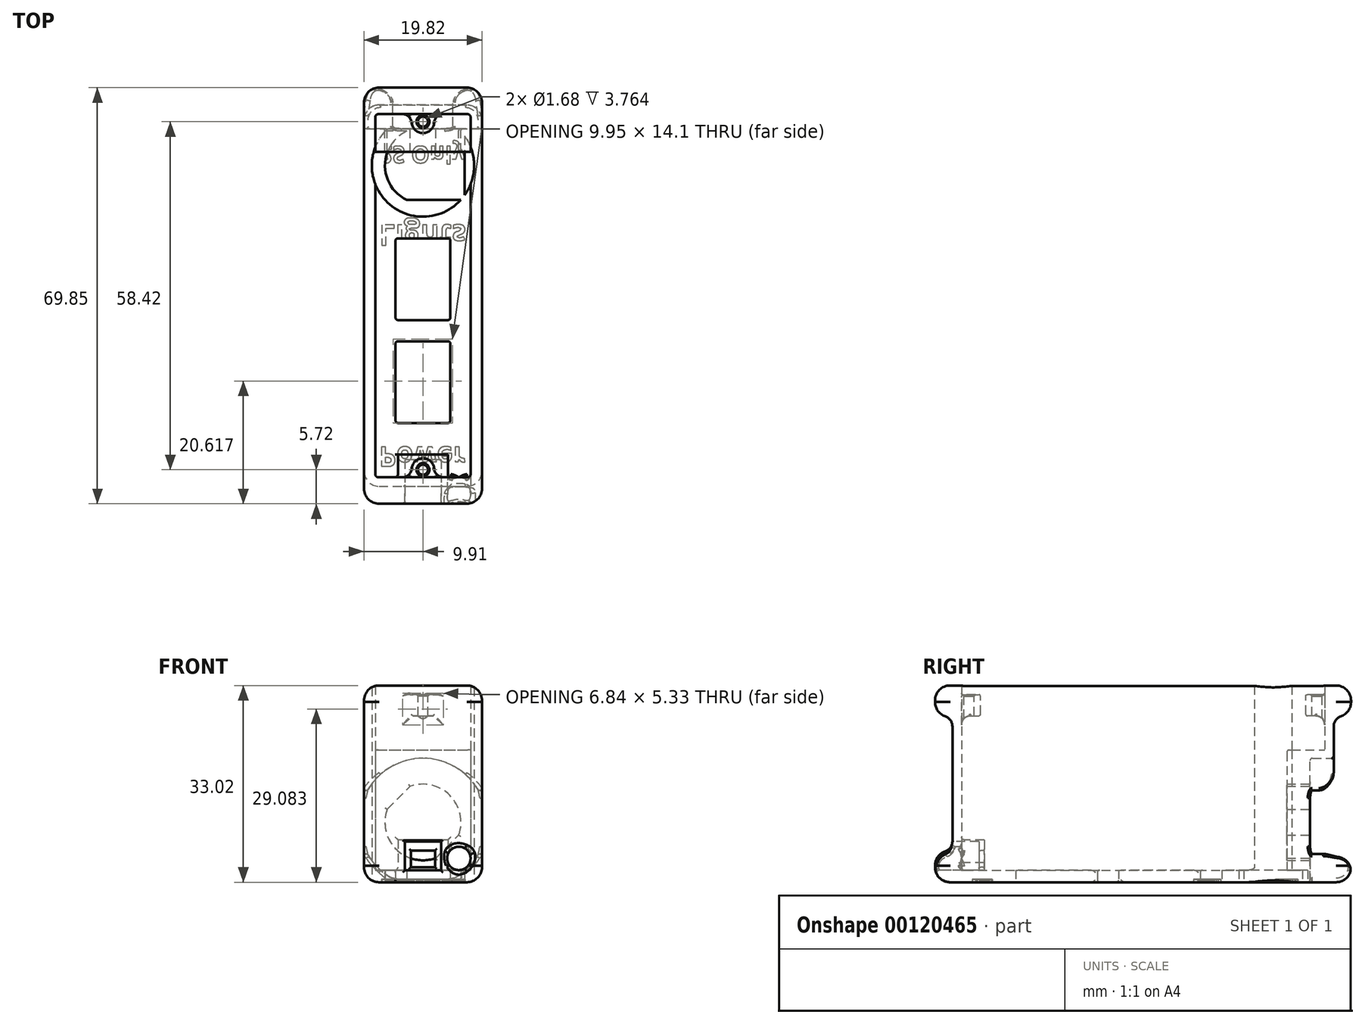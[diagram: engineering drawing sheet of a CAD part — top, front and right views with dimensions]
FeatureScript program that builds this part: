
annotation { "Feature Type Name" : "Feature", "Feature Type Description" : "" }
export const myFeature = defineFeature(function(context is Context, id is Id, definition is map)
    precondition{}
    {
        {
            var Q0;
            Q0=qCreatedBy(makeId("Top.planeOp"),FACE);
            var sketch = newSketch(context, id + "F0", { "sketchPlane" : qUnion([Q0])});
            skLineSegment(sketch, "E0.bottom", {"start": v(8, 30.48) * mm, "end": v(-8, 30.48) * mm});
            skLineSegment(sketch, "E0.top", {"start": v(8, -30.48) * mm, "end": v(-8, -30.48) * mm});
            skLineSegment(sketch, "E0.left", {"start": v(8, 30.48) * mm, "end": v(8, -30.48) * mm});
            skLineSegment(sketch, "E0.right", {"start": v(-8, 30.48) * mm, "end": v(-8, -30.48) * mm});
            skPoint(sketch, "E0.middle", {"position": v(0, 0) * mm});
            skLineSegment(sketch, "E1.bottom", {"start": v(9.9, 32.38) * mm, "end": v(-9.9, 32.38) * mm});
            skLineSegment(sketch, "E1.top", {"start": v(9.9, -32.38) * mm, "end": v(-9.9, -32.38) * mm});
            skLineSegment(sketch, "E1.left", {"start": v(9.9, 32.38) * mm, "end": v(9.9, -32.38) * mm});
            skLineSegment(sketch, "E1.right", {"start": v(-9.9, 32.38) * mm, "end": v(-9.9, -32.38) * mm});
            skCircle(sketch, "E2", {"center": v(0, 21.84) * mm, "radius": 6.38 * mm});
            skLineSegment(sketch, "E3.bottom", {"start": v(7.02, 27.62) * mm, "end": v(-7.02, 27.62) * mm});
            skLineSegment(sketch, "E3.top", {"start": v(7.02, 16.07) * mm, "end": v(-7.02, 16.07) * mm});
            skLineSegment(sketch, "E3.left", {"start": v(7.02, 27.62) * mm, "end": v(7.02, 16.07) * mm});
            skLineSegment(sketch, "E3.right", {"start": v(-7.02, 27.62) * mm, "end": v(-7.02, 16.07) * mm});
            skLineSegment(sketch, "E4.bottom", {"start": v(4.6, 9.63) * mm, "end": v(-4.6, 9.63) * mm});
            skLineSegment(sketch, "E4.top", {"start": v(4.6, -4.09) * mm, "end": v(-4.6, -4.09) * mm});
            skLineSegment(sketch, "E4.left", {"start": v(4.6, 9.63) * mm, "end": v(4.6, -4.09) * mm});
            skLineSegment(sketch, "E4.right", {"start": v(-4.6, 9.63) * mm, "end": v(-4.6, -4.09) * mm});
            skPoint(sketch, "E4.middle", {"position": v(0, 2.77) * mm});
            skCircle(sketch, "E5", {"center": v(0, 21.84) * mm, "radius": 8.59 * mm});
            skLineSegment(sketch, "E6.bottom", {"start": v(4.6, -7.65) * mm, "end": v(-4.6, -7.65) * mm});
            skLineSegment(sketch, "E6.top", {"start": v(4.6, -21.36) * mm, "end": v(-4.6, -21.36) * mm});
            skLineSegment(sketch, "E6.left", {"start": v(4.6, -7.65) * mm, "end": v(4.6, -21.36) * mm});
            skLineSegment(sketch, "E6.right", {"start": v(-4.6, -7.65) * mm, "end": v(-4.6, -21.36) * mm});
            skPoint(sketch, "E6.middle", {"position": v(0, -14.5) * mm});
            skSolve(sketch);
        }
        {
            var Q0;
            Q0 = qSketchRegion(id + "F0", true);
            var Q1;
            {var subQ0=sQuery(id+"F0.wireOp",EDGE,"E5");var subQ1=sQuery(id+"F0.wireOp",EDGE,"E0.right");var subQ2=makeQuery(id+"F0.imprint","INTERSECT",VERTEX,{"disambiguationData":[OD(0.0)],"derivedFrom":[subQ1,subQ0]});Q1=makeQuery(id+"F0.imprint","IMPRINT",FACE,{"disambiguationData":[TD([[makeQuery(id+"F0.imprint","IMPRINT",EDGE,{"disambiguationData":[TD([[subQ2,-1.0]])],"derivedFrom":subQ1}),-1.0]])]});}
            var Q2;
            {var subQ0=sQuery(id+"F0.wireOp",EDGE,"E5");var subQ1=sQuery(id+"F0.wireOp",EDGE,"E0.left");var subQ2=makeQuery(id+"F0.imprint","INTERSECT",VERTEX,{"disambiguationData":[OD(0.0)],"derivedFrom":[subQ1,subQ0]});Q2=makeQuery(id+"F0.imprint","IMPRINT",FACE,{"disambiguationData":[TD([[makeQuery(id+"F0.imprint","IMPRINT",EDGE,{"disambiguationData":[TD([[subQ2,-1.0]])],"derivedFrom":subQ1}),1.0]])]});}
            var Q3;
            {var subQ1=sQuery(id+"F0.wireOp",EDGE,"E0.bottom");Q3=makeQuery(id+"F0.imprint","IMPRINT",FACE,{"disambiguationData":[TD([[makeQuery(id+"F0.imprint","IMPRINT",EDGE,{"derivedFrom":subQ1}),1.0]])]});}
            var Q4;
            {var subQ0=sQuery(id+"F0.wireOp",EDGE,"E3.bottom");var subQ1=sQuery(id+"F0.wireOp",EDGE,"E2");var subQ2=makeQuery(id+"F0.imprint","INTERSECT",VERTEX,{"disambiguationData":[OD(0.0)],"derivedFrom":[subQ1,subQ0]});Q4=makeQuery(id+"F0.imprint","IMPRINT",FACE,{"disambiguationData":[TD([[makeQuery(id+"F0.imprint","IMPRINT",EDGE,{"disambiguationData":[TD([[subQ2,1.0]])],"derivedFrom":subQ1}),-1.0]])]});}
            var Q5;
            {var subQ0=sQuery(id+"F0.wireOp",EDGE,"E3.bottom");var subQ1=sQuery(id+"F0.wireOp",EDGE,"E2");var subQ2=makeQuery(id+"F0.imprint","INTERSECT",VERTEX,{"disambiguationData":[OD(0.0)],"derivedFrom":[subQ1,subQ0]});Q5=makeQuery(id+"F0.imprint","IMPRINT",FACE,{"disambiguationData":[TD([[makeQuery(id+"F0.imprint","IMPRINT",EDGE,{"disambiguationData":[TD([[subQ2,1.0]])],"derivedFrom":subQ1}),1.0]])]});}
            var Q6;
            {var subQ1=sQuery(id+"F0.wireOp",EDGE,"E2");var subQ5=sQuery(id+"F0.wireOp",EDGE,"E3.bottom");var subQ6=makeQuery(id+"F0.imprint","INTERSECT",VERTEX,{"disambiguationData":[OD(0.0)],"derivedFrom":[subQ1,subQ5]});Q6=makeQuery(id+"F0.imprint","IMPRINT",FACE,{"disambiguationData":[TD([[makeQuery(id+"F0.imprint","IMPRINT",EDGE,{"disambiguationData":[TD([[subQ6,-1.0]])],"derivedFrom":subQ1}),-1.0]])]});}
            var Q7;
            {var subQ0=sQuery(id+"F0.wireOp",EDGE,"E5");var subQ1=sQuery(id+"F0.wireOp",EDGE,"E0.right");var subQ2=makeQuery(id+"F0.imprint","INTERSECT",VERTEX,{"disambiguationData":[OD(0.0)],"derivedFrom":[subQ1,subQ0]});Q7=makeQuery(id+"F0.imprint","IMPRINT",FACE,{"disambiguationData":[TD([[makeQuery(id+"F0.imprint","IMPRINT",EDGE,{"disambiguationData":[TD([[subQ2,-1.0]])],"derivedFrom":subQ1}),1.0]])]});}
            var Q8;
            {var subQ0=sQuery(id+"F0.wireOp",EDGE,"E3.top");var subQ1=sQuery(id+"F0.wireOp",EDGE,"E2");var subQ2=makeQuery(id+"F0.imprint","INTERSECT",VERTEX,{"disambiguationData":[OD(0.0)],"derivedFrom":[subQ1,subQ0]});Q8=makeQuery(id+"F0.imprint","IMPRINT",FACE,{"disambiguationData":[TD([[makeQuery(id+"F0.imprint","IMPRINT",EDGE,{"disambiguationData":[TD([[subQ2,-1.0]])],"derivedFrom":subQ1}),-1.0]])]});}
            var Q9;
            {var subQ0=sQuery(id+"F0.wireOp",EDGE,"E3.right");var subQ1=sQuery(id+"F0.wireOp",EDGE,"E3.top");var subQ2=makeQuery(id+"F0.imprint","INTERSECT",VERTEX,{"derivedFrom":[subQ1,subQ0]});Q9=makeQuery(id+"F0.imprint","IMPRINT",FACE,{"disambiguationData":[TD([[makeQuery(id+"F0.imprint","IMPRINT",EDGE,{"disambiguationData":[TD([[subQ2,1.0]])],"derivedFrom":subQ1}),-1.0]])]});}
            var Q10;
            {var subQ0=sQuery(id+"F0.wireOp",EDGE,"E3.right");var subQ1=sQuery(id+"F0.wireOp",EDGE,"E3.bottom");var subQ2=makeQuery(id+"F0.imprint","INTERSECT",VERTEX,{"derivedFrom":[subQ1,subQ0]});Q10=makeQuery(id+"F0.imprint","IMPRINT",FACE,{"disambiguationData":[TD([[makeQuery(id+"F0.imprint","IMPRINT",EDGE,{"disambiguationData":[TD([[subQ2,1.0]])],"derivedFrom":subQ1}),1.0]])]});}
            var Q11;
            {var subQ0=sQuery(id+"F0.wireOp",EDGE,"E3.left");var subQ1=sQuery(id+"F0.wireOp",EDGE,"E3.bottom");var subQ2=makeQuery(id+"F0.imprint","INTERSECT",VERTEX,{"derivedFrom":[subQ1,subQ0]});Q11=makeQuery(id+"F0.imprint","IMPRINT",FACE,{"disambiguationData":[TD([[makeQuery(id+"F0.imprint","IMPRINT",EDGE,{"disambiguationData":[TD([[subQ2,-1.0]])],"derivedFrom":subQ1}),1.0]])]});}
            var Q12;
            {var subQ0=sQuery(id+"F0.wireOp",EDGE,"E5");var subQ1=sQuery(id+"F0.wireOp",EDGE,"E0.left");var subQ2=makeQuery(id+"F0.imprint","INTERSECT",VERTEX,{"disambiguationData":[OD(0.0)],"derivedFrom":[subQ1,subQ0]});Q12=makeQuery(id+"F0.imprint","IMPRINT",FACE,{"disambiguationData":[TD([[makeQuery(id+"F0.imprint","IMPRINT",EDGE,{"disambiguationData":[TD([[subQ2,-1.0]])],"derivedFrom":subQ1}),-1.0]])]});}
            var Q13;
            {var subQ1=sQuery(id+"F0.wireOp",EDGE,"E2");var subQ5=sQuery(id+"F0.wireOp",EDGE,"E3.bottom");var subQ6=makeQuery(id+"F0.imprint","INTERSECT",VERTEX,{"disambiguationData":[OD(1.0)],"derivedFrom":[subQ1,subQ5]});Q13=makeQuery(id+"F0.imprint","IMPRINT",FACE,{"disambiguationData":[TD([[makeQuery(id+"F0.imprint","IMPRINT",EDGE,{"disambiguationData":[TD([[subQ6,1.0]])],"derivedFrom":subQ1}),-1.0]])]});}
            var Q14;
            {var subQ0=sQuery(id+"F0.wireOp",EDGE,"E3.top");var subQ1=sQuery(id+"F0.wireOp",EDGE,"E2");var subQ2=makeQuery(id+"F0.imprint","INTERSECT",VERTEX,{"disambiguationData":[OD(0.0)],"derivedFrom":[subQ1,subQ0]});Q14=makeQuery(id+"F0.imprint","IMPRINT",FACE,{"disambiguationData":[TD([[makeQuery(id+"F0.imprint","IMPRINT",EDGE,{"disambiguationData":[TD([[subQ2,-1.0]])],"derivedFrom":subQ1}),1.0]])]});}
            var Q15;
            {var subQ0=sQuery(id+"F0.wireOp",EDGE,"E3.left");var subQ1=sQuery(id+"F0.wireOp",EDGE,"E3.top");var subQ2=makeQuery(id+"F0.imprint","INTERSECT",VERTEX,{"derivedFrom":[subQ1,subQ0]});Q15=makeQuery(id+"F0.imprint","IMPRINT",FACE,{"disambiguationData":[TD([[makeQuery(id+"F0.imprint","IMPRINT",EDGE,{"disambiguationData":[TD([[subQ2,-1.0]])],"derivedFrom":subQ1}),-1.0]])]});}
            var Q16;
            {var subQ8=sQuery(id+"F0.wireOp",EDGE,"E0.top");Q16=makeQuery(id+"F0.imprint","IMPRINT",FACE,{"disambiguationData":[TD([[makeQuery(id+"F0.imprint","IMPRINT",EDGE,{"derivedFrom":subQ8}),-1.0]])]});}
            var Q17;
            {var subQ0=sQuery(id+"F0.wireOp",EDGE,"E3.bottom");var subQ1=sQuery(id+"F0.wireOp",EDGE,"E2");var subQ2=makeQuery(id+"F0.imprint","INTERSECT",VERTEX,{"disambiguationData":[OD(0.0)],"derivedFrom":[subQ1,subQ0]});Q17=makeQuery(id+"F0.imprint","IMPRINT",FACE,{"disambiguationData":[TD([[makeQuery(id+"F0.imprint","IMPRINT",EDGE,{"disambiguationData":[TD([[subQ2,-1.0]])],"derivedFrom":subQ1}),1.0]])]});}
            extrude(context, id + "F1", {"entities" : qUnion([Q0, Q1, Q2, Q3, Q4, Q5, Q6, Q7, Q8, Q9, Q10, Q11, Q12, Q13, Q14, Q15, Q16, Q17]), "depth" : 2.03 * mm});
        }
        {
            var Q0;
            {var subQ4=sQuery(id+"F0.wireOp",EDGE,"E0.bottom");Q0=makeQuery(id+"F0.imprint","IMPRINT",FACE,{"disambiguationData":[TD([[makeQuery(id+"F0.imprint","IMPRINT",EDGE,{"derivedFrom":subQ4}),-1.0]])]});}
            var Q1;
            {var subQ0=sQuery(id+"F0.wireOp",EDGE,"E5");var subQ1=sQuery(id+"F0.wireOp",EDGE,"E0.left");var subQ2=makeQuery(id+"F0.imprint","INTERSECT",VERTEX,{"disambiguationData":[OD(0.0)],"derivedFrom":[subQ1,subQ0]});Q1=makeQuery(id+"F0.imprint","IMPRINT",FACE,{"disambiguationData":[TD([[makeQuery(id+"F0.imprint","IMPRINT",EDGE,{"disambiguationData":[TD([[subQ2,-1.0]])],"derivedFrom":subQ1}),1.0]])]});}
            var Q2;
            {var subQ0=sQuery(id+"F0.wireOp",EDGE,"E5");var subQ1=sQuery(id+"F0.wireOp",EDGE,"E0.right");var subQ2=makeQuery(id+"F0.imprint","INTERSECT",VERTEX,{"disambiguationData":[OD(0.0)],"derivedFrom":[subQ1,subQ0]});Q2=makeQuery(id+"F0.imprint","IMPRINT",FACE,{"disambiguationData":[TD([[makeQuery(id+"F0.imprint","IMPRINT",EDGE,{"disambiguationData":[TD([[subQ2,-1.0]])],"derivedFrom":subQ1}),-1.0]])]});}
            extrude(context, id + "F2", {"entities" : qUnion([Q0, Q1, Q2]), "operationType" : NewBodyOperationType.ADD, "depth" : 33.02 * mm});
        }
        {
            var Q0;
            Q0=makeQuery(id+"F2.opExtrude","CAP_FACE",FACE,{"disambiguationData":[OSD([sQuery(id+"F0.wireOp",EDGE,"E0.bottom"),sQuery(id+"F0.wireOp",EDGE,"E0.top"),sQuery(id+"F0.wireOp",EDGE,"E0.left"),sQuery(id+"F0.wireOp",EDGE,"E0.right"),sQuery(id+"F0.wireOp",EDGE,"E1.bottom"),sQuery(id+"F0.wireOp",EDGE,"E1.top"),sQuery(id+"F0.wireOp",EDGE,"E1.left"),sQuery(id+"F0.wireOp",EDGE,"E1.right")])],"isStart":false});
            var sketch = newSketch(context, id + "F3", { "sketchPlane" : qUnion([Q0])});
            skCircle(sketch, "E7", {"center": v(0, 29.21) * mm, "radius": 1.9 * mm});
            skCircle(sketch, "E8", {"center": v(0, -29.21) * mm, "radius": 1.9 * mm});
            skCircle(sketch, "E9", {"center": v(0, -29.21) * mm, "radius": 0.84 * mm});
            skCircle(sketch, "E10", {"center": v(0, 29.21) * mm, "radius": 0.84 * mm});
            skSolve(sketch);
        }
        {
            var Q0;
            Q0 = qSketchRegion(id + "F3", true);
            extrude(context, id + "F4", {"entities" : qUnion([Q0]), "operationType" : NewBodyOperationType.ADD, "oppositeDirection" : true, "depth" : 5.08 * mm});
        }
        {
            var Q0;
            {var subQ0=sQuery(id+"F0.wireOp",EDGE,"E1.bottom");Q0=makeQuery(id+"F2.boolean.opBoolean","MERGE",FACE,{"derivedFrom":[makeQuery(id+"F1.opExtrude","SWEPT_FACE",FACE,{"disambiguationData":[OSD([subQ0])]}),makeQuery(id+"F2.opExtrude","SWEPT_FACE",FACE,{"disambiguationData":[OSD([subQ0])]})]});}
            extrude(context, id + "F5", {"entities" : qUnion([Q0]), "operationType" : NewBodyOperationType.ADD, "depth" : 2.54 * mm});
        }
        {
            var Q0;
            {var subQ0=sQuery(id+"F0.wireOp",EDGE,"E1.top");Q0=makeQuery(id+"F2.boolean.opBoolean","MERGE",FACE,{"derivedFrom":[makeQuery(id+"F1.opExtrude","SWEPT_FACE",FACE,{"disambiguationData":[OSD([subQ0])]}),makeQuery(id+"F2.opExtrude","SWEPT_FACE",FACE,{"disambiguationData":[OSD([subQ0])]})]});}
            extrude(context, id + "F6", {"entities" : qUnion([Q0]), "operationType" : NewBodyOperationType.ADD, "depth" : 2.54 * mm});
        }
        {
            var Q0;
            Q0=qCreatedBy(makeId("Right.planeOp"),FACE);
            var sketch = newSketch(context, id + "F7", { "sketchPlane" : qUnion([Q0])});
            skLineSegment(sketch, "E11.bottom", {"start": v(38.48, 27.94) * mm, "end": v(33.78, 27.94) * mm});
            skLineSegment(sketch, "E11.top", {"start": v(38.48, 5.08) * mm, "end": v(33.78, 5.08) * mm});
            skLineSegment(sketch, "E11.left", {"start": v(38.48, 27.94) * mm, "end": v(38.48, 5.08) * mm});
            skLineSegment(sketch, "E11.right", {"start": v(32, 26.16) * mm, "end": v(32, 6.86) * mm});
            skLineSegment(sketch, "E12.bottom", {"start": v(-39.14, 27.94) * mm, "end": v(-33.78, 27.94) * mm});
            skLineSegment(sketch, "E12.top", {"start": v(-39.14, 5.08) * mm, "end": v(-33.78, 5.08) * mm});
            skLineSegment(sketch, "E12.left", {"start": v(-39.14, 27.94) * mm, "end": v(-39.14, 5.08) * mm});
            skLineSegment(sketch, "E12.right", {"start": v(-32, 26.16) * mm, "end": v(-32, 6.86) * mm});
            skPoint(sketch, "E13.visualSharp", {"position": v(32, 27.94) * mm});
            skArc(sketch, "E13.filletArc", {"start": v(33.78, 27.94) * mm, "mid": v(32.52, 27.42) * mm, "end": v(32, 26.16) * mm});
            skPoint(sketch, "E14.visualSharp", {"position": v(32, 5.08) * mm});
            skArc(sketch, "E14.filletArc", {"start": v(32, 6.86) * mm, "mid": v(32.52, 5.6) * mm, "end": v(33.78, 5.08) * mm});
            skPoint(sketch, "E15.visualSharp", {"position": v(-32, 5.08) * mm});
            skArc(sketch, "E15.filletArc", {"start": v(-33.78, 5.08) * mm, "mid": v(-32.52, 5.6) * mm, "end": v(-32, 6.86) * mm});
            skPoint(sketch, "E16.visualSharp", {"position": v(-32, 27.94) * mm});
            skArc(sketch, "E16.filletArc", {"start": v(-32, 26.16) * mm, "mid": v(-32.52, 27.42) * mm, "end": v(-33.78, 27.94) * mm});
            skSolve(sketch);
        }
        {
            var Q0;
            Q0 = qSketchRegion(id + "F7", true);
            extrude(context, id + "F8", {"entities" : qUnion([Q0]), "operationType" : NewBodyOperationType.REMOVE, "endBound" : BoundingType.SYMMETRIC, "oppositeDirection" : true, "depth" : 25.4 * mm});
        }
        {
            var Q0;
            Q0=makeQuery(id+"F2.opExtrude","SWEPT_FACE",FACE,{"disambiguationData":[OSD([sQuery(id+"F0.wireOp",EDGE,"E0.bottom")])]});
            var sketch = newSketch(context, id + "F9", { "sketchPlane" : qUnion([Q0])});
            skCircle(sketch, "E17", {"center": v(0, 10.07) * mm, "radius": 6.39 * mm});
            skLineSegment(sketch, "E18.bottom", {"start": v(-8, 2.03) * mm, "end": v(8, 2.03) * mm});
            skLineSegment(sketch, "E18.top", {"start": v(-8, 22.17) * mm, "end": v(8, 22.17) * mm});
            skLineSegment(sketch, "E18.left", {"start": v(-8, 2.03) * mm, "end": v(-8, 22.17) * mm});
            skLineSegment(sketch, "E18.right", {"start": v(8, 2.03) * mm, "end": v(8, 22.17) * mm});
            skSolve(sketch);
        }
        {
            var Q0;
            Q0=qCreatedBy(makeId("Front.planeOp"),FACE);
            cPlane(context, id + "F10", {"entities" : qUnion([Q0]), "cplaneType" : CPlaneType.OFFSET, "offset" : 38.1 * mm, "oppositeDirection" : true, "width" : 152.4 * mm, "height" : 152.4 * mm});
        }
        {
            var Q0;
            Q0=qCreatedBy(id+"F10.planeOp",FACE);
            var sketch = newSketch(context, id + "F11", { "sketchPlane" : qUnion([Q0])});
            skCircle(sketch, "E19", {"center": v(0, 10.07) * mm, "radius": 6.39 * mm});
            skCircle(sketch, "E20", {"center": v(0, 10.07) * mm, "radius": 10.73 * mm});
            skLineSegment(sketch, "E21", {"start": v(-1.17, 0.73) * mm, "end": v(9.04, 10.94) * mm});
            skLineSegment(sketch, "E22", {"start": v(-1.17, 0.73) * mm, "end": v(-9.34, 8.9) * mm});
            skLineSegment(sketch, "E23", {"start": v(-9.34, 8.9) * mm, "end": v(0.87, 19.11) * mm});
            skLineSegment(sketch, "E24", {"start": v(0.87, 19.11) * mm, "end": v(9.04, 10.94) * mm});
            skSolve(sketch);
        }
        {
            var Q0;
            {var subQ1=sQuery(id+"F0.wireOp",EDGE,"E1.left");var subQ2=sQuery(id+"F0.wireOp",EDGE,"E1.top");Q0=makeQuery(id+"F8.boolean.opBoolean","SPLIT",EDGE,{"disambiguationData":[TD([makeQuery(id+"F8.opExtrude","SWEPT_FACE",FACE,{"disambiguationData":[OSD([sQuery(id+"F7.wireOp",EDGE,"E12.top")])]})])],"derivedFrom":makeQuery(id+"F6.opExtrude","CAP_EDGE",EDGE,{"disambiguationData":[OSD([subQ2,subQ1])],"isStart":false})});}
            var Q1;
            {var subQ0=sQuery(id+"F0.wireOp",EDGE,"E1.left");var subQ1=sQuery(id+"F0.wireOp",EDGE,"E1.top");Q1=makeQuery(id+"F8.boolean.opBoolean","SPLIT",EDGE,{"disambiguationData":[TD([makeQuery(id+"F8.opExtrude","SWEPT_FACE",FACE,{"disambiguationData":[OSD([sQuery(id+"F7.wireOp",EDGE,"E12.bottom")])]})])],"derivedFrom":makeQuery(id+"F6.opExtrude","CAP_EDGE",EDGE,{"disambiguationData":[OSD([subQ1,subQ0])],"isStart":false})});}
            var Q2;
            {var subQ0=sQuery(id+"F0.wireOp",EDGE,"E1.top");var subQ1=sQuery(id+"F0.wireOp",EDGE,"E1.right");Q2=makeQuery(id+"F8.boolean.opBoolean","SPLIT",EDGE,{"disambiguationData":[TD([makeQuery(id+"F8.opExtrude","SWEPT_FACE",FACE,{"disambiguationData":[OSD([sQuery(id+"F7.wireOp",EDGE,"E12.bottom")])]})])],"derivedFrom":makeQuery(id+"F6.opExtrude","CAP_EDGE",EDGE,{"disambiguationData":[OSD([subQ0,subQ1])],"isStart":false})});}
            var Q3;
            {var subQ1=sQuery(id+"F0.wireOp",EDGE,"E1.right");var subQ2=sQuery(id+"F0.wireOp",EDGE,"E1.top");Q3=makeQuery(id+"F8.boolean.opBoolean","SPLIT",EDGE,{"disambiguationData":[TD([makeQuery(id+"F8.opExtrude","SWEPT_FACE",FACE,{"disambiguationData":[OSD([sQuery(id+"F7.wireOp",EDGE,"E12.top")])]})])],"derivedFrom":makeQuery(id+"F6.opExtrude","CAP_EDGE",EDGE,{"disambiguationData":[OSD([subQ2,subQ1])],"isStart":false})});}
            var Q4;
            {var subQ0=sQuery(id+"F0.wireOp",EDGE,"E1.bottom");var subQ1=sQuery(id+"F0.wireOp",EDGE,"E1.right");Q4=makeQuery(id+"F8.boolean.opBoolean","SPLIT",EDGE,{"disambiguationData":[TD([makeQuery(id+"F8.opExtrude","SWEPT_FACE",FACE,{"disambiguationData":[OSD([sQuery(id+"F7.wireOp",EDGE,"E11.top")])]})])],"derivedFrom":makeQuery(id+"F5.opExtrude","CAP_EDGE",EDGE,{"disambiguationData":[OSD([subQ0,subQ1])],"isStart":false})});}
            var Q5;
            {var subQ0=sQuery(id+"F0.wireOp",EDGE,"E1.bottom");var subQ1=sQuery(id+"F0.wireOp",EDGE,"E1.left");Q5=makeQuery(id+"F8.boolean.opBoolean","SPLIT",EDGE,{"disambiguationData":[TD([makeQuery(id+"F8.opExtrude","SWEPT_FACE",FACE,{"disambiguationData":[OSD([sQuery(id+"F7.wireOp",EDGE,"E11.top")])]})])],"derivedFrom":makeQuery(id+"F5.opExtrude","CAP_EDGE",EDGE,{"disambiguationData":[OSD([subQ0,subQ1])],"isStart":false})});}
            var Q6;
            {var subQ0=sQuery(id+"F0.wireOp",EDGE,"E1.right");var subQ2=sQuery(id+"F0.wireOp",EDGE,"E1.bottom");Q6=makeQuery(id+"F8.boolean.opBoolean","SPLIT",EDGE,{"disambiguationData":[TD([makeQuery(id+"F8.opExtrude","SWEPT_FACE",FACE,{"disambiguationData":[OSD([sQuery(id+"F7.wireOp",EDGE,"E11.bottom")])]})])],"derivedFrom":makeQuery(id+"F5.opExtrude","CAP_EDGE",EDGE,{"disambiguationData":[OSD([subQ2,subQ0])],"isStart":false})});}
            var Q7;
            {var subQ0=sQuery(id+"F0.wireOp",EDGE,"E1.left");var subQ2=sQuery(id+"F0.wireOp",EDGE,"E1.bottom");Q7=makeQuery(id+"F8.boolean.opBoolean","SPLIT",EDGE,{"disambiguationData":[TD([makeQuery(id+"F8.opExtrude","SWEPT_FACE",FACE,{"disambiguationData":[OSD([sQuery(id+"F7.wireOp",EDGE,"E11.bottom")])]})])],"derivedFrom":makeQuery(id+"F5.opExtrude","CAP_EDGE",EDGE,{"disambiguationData":[OSD([subQ2,subQ0])],"isStart":false})});}
            fillet(context, id + "F12", {"entities" : qUnion([Q0, Q1, Q2, Q3, Q4, Q5, Q6, Q7]), "radius" : 2.54 * mm, "tangentPropagation" : true, "allowEdgeOverflow" : false});
        }
        {
            var Q0;
            Q0 = qSketchRegion(id + "F9", true);
            var Q1;
            Q1=makeQuery(id+"F9.imprint","IMPRINT",FACE,{"disambiguationData":[TD([[makeQuery(id+"F9.imprint","IMPRINT",EDGE,{"derivedFrom":sQuery(id+"F9.wireOp",EDGE,"E17")}),1.0]])]});
            extrude(context, id + "F13", {"entities" : qUnion([Q0, Q1]), "operationType" : NewBodyOperationType.ADD, "depth" : 6.35 * mm});
        }
        {
            var Q0;
            Q0=makeQuery(id+"F11.imprint","IMPRINT",FACE,{"disambiguationData":[TD([[makeQuery(id+"F11.imprint","IMPRINT",EDGE,{"derivedFrom":sQuery(id+"F11.wireOp",EDGE,"E19")}),1.0]])]});
            var Q1;
            Q1=makeQuery(id+"F13.opExtrude","CAP_FACE",FACE,{"disambiguationData":[OSD([sQuery(id+"F9.wireOp",EDGE,"E18.bottom"),sQuery(id+"F9.wireOp",EDGE,"E18.top"),sQuery(id+"F9.wireOp",EDGE,"E18.left"),sQuery(id+"F9.wireOp",EDGE,"E18.right")])],"isStart":false});
            extrude(context, id + "F14", {"entities" : qUnion([Q0]), "operationType" : NewBodyOperationType.REMOVE, "endBound" : BoundingType.UP_TO_SURFACE, "endBoundEntityFace" : qUnion([Q1]), "depth" : 25.4 * mm});
        }
        {
            var Q0;
            {var subQ0=sQuery(id+"F0.wireOp",EDGE,"E1.right");Q0=makeQuery(id+"F8.boolean.opBoolean","INTERSECT",EDGE,{"derivedFrom":[makeQuery(id+"F6.boolean.opBoolean","MERGE",FACE,{"derivedFrom":[makeQuery(id+"F5.boolean.opBoolean","MERGE",FACE,{"derivedFrom":[makeQuery(id+"F2.boolean.opBoolean","MERGE",FACE,{"derivedFrom":[makeQuery(id+"F1.opExtrude","SWEPT_FACE",FACE,{"disambiguationData":[OSD([subQ0])]}),makeQuery(id+"F2.opExtrude","SWEPT_FACE",FACE,{"disambiguationData":[OSD([subQ0])]})]}),makeQuery(id+"F5.opExtrude","SWEPT_FACE",FACE,{"disambiguationData":[OSD([sQuery(id+"F0.wireOp",EDGE,"E1.bottom"),subQ0])]})]}),makeQuery(id+"F6.opExtrude","SWEPT_FACE",FACE,{"disambiguationData":[OSD([sQuery(id+"F0.wireOp",EDGE,"E1.top"),subQ0])]})]}),makeQuery(id+"F8.opExtrude","SWEPT_FACE",FACE,{"disambiguationData":[OSD([sQuery(id+"F7.wireOp",EDGE,"E11.right")])]})]});}
            var Q1;
            {var subQ0=sQuery(id+"F0.wireOp",EDGE,"E1.right");Q1=makeQuery(id+"F8.boolean.opBoolean","INTERSECT",EDGE,{"derivedFrom":[makeQuery(id+"F6.boolean.opBoolean","MERGE",FACE,{"derivedFrom":[makeQuery(id+"F5.boolean.opBoolean","MERGE",FACE,{"derivedFrom":[makeQuery(id+"F2.boolean.opBoolean","MERGE",FACE,{"derivedFrom":[makeQuery(id+"F1.opExtrude","SWEPT_FACE",FACE,{"disambiguationData":[OSD([subQ0])]}),makeQuery(id+"F2.opExtrude","SWEPT_FACE",FACE,{"disambiguationData":[OSD([subQ0])]})]}),makeQuery(id+"F5.opExtrude","SWEPT_FACE",FACE,{"disambiguationData":[OSD([sQuery(id+"F0.wireOp",EDGE,"E1.bottom"),subQ0])]})]}),makeQuery(id+"F6.opExtrude","SWEPT_FACE",FACE,{"disambiguationData":[OSD([sQuery(id+"F0.wireOp",EDGE,"E1.top"),subQ0])]})]}),makeQuery(id+"F8.opExtrude","SWEPT_FACE",FACE,{"disambiguationData":[OSD([sQuery(id+"F7.wireOp",EDGE,"E12.right")])]})]});}
            fillet(context, id + "F15", {"entities" : qUnion([Q0, Q1]), "radius" : 2.54 * mm, "tangentPropagation" : true, "allowEdgeOverflow" : false});
        }
        {
            var Q0;
            {var subQ0=sQuery(id+"F0.wireOp",EDGE,"E1.left");var subQ1=sQuery(id+"F0.wireOp",EDGE,"E1.top");var subQ2=sQuery(id+"F0.wireOp",EDGE,"E1.bottom");Q0=makeQuery(id+"F6.boolean.opBoolean","MERGE",EDGE,{"derivedFrom":[makeQuery(id+"F5.boolean.opBoolean","MERGE",EDGE,{"derivedFrom":[makeQuery(id+"F2.opExtrude","CAP_EDGE",EDGE,{"disambiguationData":[OSD([subQ0])],"isStart":false}),makeQuery(id+"F5.opExtrude","SWEPT_EDGE",EDGE,{"disambiguationData":[OSD([subQ2,subQ0]),TDD([makeQuery(id+"F2.opExtrude","CAP_VERTEX",VERTEX,{"disambiguationData":[OSD([subQ2,subQ0])],"isStart":false})])]})]}),makeQuery(id+"F6.opExtrude","SWEPT_EDGE",EDGE,{"disambiguationData":[OSD([subQ1,subQ0]),TDD([makeQuery(id+"F2.opExtrude","CAP_VERTEX",VERTEX,{"disambiguationData":[OSD([subQ1,subQ0])],"isStart":false})])]})]});}
            var Q1;
            {var subQ0=sQuery(id+"F0.wireOp",EDGE,"E1.right");var subQ1=sQuery(id+"F0.wireOp",EDGE,"E1.top");var subQ2=sQuery(id+"F0.wireOp",EDGE,"E1.bottom");Q1=makeQuery(id+"F6.boolean.opBoolean","MERGE",EDGE,{"derivedFrom":[makeQuery(id+"F5.boolean.opBoolean","MERGE",EDGE,{"derivedFrom":[makeQuery(id+"F1.opExtrude","CAP_EDGE",EDGE,{"disambiguationData":[OSD([subQ0])],"isStart":true}),makeQuery(id+"F5.opExtrude","SWEPT_EDGE",EDGE,{"disambiguationData":[OSD([subQ2,subQ0]),TDD([makeQuery(id+"F1.opExtrude","CAP_VERTEX",VERTEX,{"disambiguationData":[OSD([subQ2,subQ0])],"isStart":true})])]})]}),makeQuery(id+"F6.opExtrude","SWEPT_EDGE",EDGE,{"disambiguationData":[OSD([subQ1,subQ0]),TDD([makeQuery(id+"F1.opExtrude","CAP_VERTEX",VERTEX,{"disambiguationData":[OSD([subQ1,subQ0])],"isStart":true})])]})]});}
            fillet(context, id + "F16", {"entities" : qUnion([Q0, Q1]), "radius" : 2.54 * mm, "tangentPropagation" : true, "allowEdgeOverflow" : false});
        }
        {
            var Q0;
            Q0 = qSketchRegion(id + "F11", true);
            var Q1;
            {var subQ5=sQuery(id+"F11.wireOp",EDGE,"E22");Q1=makeQuery(id+"F11.imprint","IMPRINT",FACE,{"disambiguationData":[TD([[makeQuery(id+"F11.imprint","IMPRINT",EDGE,{"derivedFrom":subQ5}),-1.0]])]});}
            var Q2;
            {var subQ5=sQuery(id+"F11.wireOp",EDGE,"E24");Q2=makeQuery(id+"F11.imprint","IMPRINT",FACE,{"disambiguationData":[TD([[makeQuery(id+"F11.imprint","IMPRINT",EDGE,{"derivedFrom":subQ5}),-1.0]])]});}
            var Q3;
            {var subQ0=sQuery(id+"F11.wireOp",EDGE,"E21");var subQ1=sQuery(id+"F11.wireOp",EDGE,"E19");var subQ2=makeQuery(id+"F11.imprint","INTERSECT",VERTEX,{"disambiguationData":[OD(0.0)],"derivedFrom":[subQ1,subQ0]});Q3=makeQuery(id+"F11.imprint","IMPRINT",FACE,{"disambiguationData":[TD([[makeQuery(id+"F11.imprint","IMPRINT",EDGE,{"disambiguationData":[TD([[subQ2,-1.0]])],"derivedFrom":subQ1}),1.0]])]});}
            var Q4;
            {var subQ0=sQuery(id+"F11.wireOp",EDGE,"E23");var subQ1=sQuery(id+"F11.wireOp",EDGE,"E19");var subQ2=makeQuery(id+"F11.imprint","INTERSECT",VERTEX,{"disambiguationData":[OD(0.0)],"derivedFrom":[subQ1,subQ0]});Q4=makeQuery(id+"F11.imprint","IMPRINT",FACE,{"disambiguationData":[TD([[makeQuery(id+"F11.imprint","IMPRINT",EDGE,{"disambiguationData":[TD([[subQ2,1.0]])],"derivedFrom":subQ1}),1.0]])]});}
            var Q5;
            {var subQ0=sQuery(id+"F11.wireOp",EDGE,"E23");var subQ1=sQuery(id+"F11.wireOp",EDGE,"E19");var subQ2=makeQuery(id+"F11.imprint","INTERSECT",VERTEX,{"disambiguationData":[OD(0.0)],"derivedFrom":[subQ1,subQ0]});Q5=makeQuery(id+"F11.imprint","IMPRINT",FACE,{"disambiguationData":[TD([[makeQuery(id+"F11.imprint","IMPRINT",EDGE,{"disambiguationData":[TD([[subQ2,-1.0]])],"derivedFrom":subQ1}),1.0]])]});}
            extrude(context, id + "F17", {"entities" : qUnion([Q0, Q1, Q2, Q3, Q4, Q5]), "operationType" : NewBodyOperationType.REMOVE, "depth" : 10.06 * mm});
        }
        {
            var Q0;
            Q0=makeQuery(id+"F4.boolean.opBoolean","INTERSECT",EDGE,{"disambiguationData":[OD(0.0)],"derivedFrom":[makeQuery(id+"F2.opExtrude","SWEPT_FACE",FACE,{"disambiguationData":[OSD([sQuery(id+"F0.wireOp",EDGE,"E0.bottom")])]}),makeQuery(id+"F4.opExtrude","SWEPT_FACE",FACE,{"disambiguationData":[OSD([sQuery(id+"F3.wireOp",EDGE,"E7")])]})]});
            var Q1;
            Q1=makeQuery(id+"F4.boolean.opBoolean","INTERSECT",EDGE,{"disambiguationData":[OD(1.0)],"derivedFrom":[makeQuery(id+"F2.opExtrude","SWEPT_FACE",FACE,{"disambiguationData":[OSD([sQuery(id+"F0.wireOp",EDGE,"E0.bottom")])]}),makeQuery(id+"F4.opExtrude","SWEPT_FACE",FACE,{"disambiguationData":[OSD([sQuery(id+"F3.wireOp",EDGE,"E7")])]})]});
            var Q2;
            Q2=makeQuery(id+"F4.boolean.opBoolean","INTERSECT",EDGE,{"disambiguationData":[OD(0.0)],"derivedFrom":[makeQuery(id+"F2.opExtrude","SWEPT_FACE",FACE,{"disambiguationData":[OSD([sQuery(id+"F0.wireOp",EDGE,"E0.top")])]}),makeQuery(id+"F4.opExtrude","SWEPT_FACE",FACE,{"disambiguationData":[OSD([sQuery(id+"F3.wireOp",EDGE,"E8")])]})]});
            var Q3;
            Q3=makeQuery(id+"F4.boolean.opBoolean","INTERSECT",EDGE,{"disambiguationData":[OD(1.0)],"derivedFrom":[makeQuery(id+"F2.opExtrude","SWEPT_FACE",FACE,{"disambiguationData":[OSD([sQuery(id+"F0.wireOp",EDGE,"E0.top")])]}),makeQuery(id+"F4.opExtrude","SWEPT_FACE",FACE,{"disambiguationData":[OSD([sQuery(id+"F3.wireOp",EDGE,"E8")])]})]});
            var Q4;
            Q4=makeQuery(id+"F4.boolean.opBoolean","INTERSECT",EDGE,{"derivedFrom":[makeQuery(id+"F2.opExtrude","SWEPT_FACE",FACE,{"disambiguationData":[OSD([sQuery(id+"F0.wireOp",EDGE,"E0.top")])]}),makeQuery(id+"F4.opExtrude","CAP_FACE",FACE,{"disambiguationData":[OSD([sQuery(id+"F3.wireOp",EDGE,"E8"),sQuery(id+"F3.wireOp",EDGE,"E9")])],"isStart":false})]});
            var Q5;
            Q5=makeQuery(id+"F4.boolean.opBoolean","INTERSECT",EDGE,{"derivedFrom":[makeQuery(id+"F2.opExtrude","SWEPT_FACE",FACE,{"disambiguationData":[OSD([sQuery(id+"F0.wireOp",EDGE,"E0.bottom")])]}),makeQuery(id+"F4.opExtrude","CAP_FACE",FACE,{"disambiguationData":[OSD([sQuery(id+"F3.wireOp",EDGE,"E7"),sQuery(id+"F3.wireOp",EDGE,"E10")])],"isStart":false})]});
            fillet(context, id + "F18", {"entities" : qUnion([Q0, Q1, Q2, Q3, Q4, Q5]), "radius" : 1.52 * mm, "tangentPropagation" : true, "allowEdgeOverflow" : false});
        }
        {
            var Q0;
            Q0=makeQuery(id+"F1.opExtrude","SWEPT_EDGE",EDGE,{"disambiguationData":[OSD([sQuery(id+"F0.wireOp",EDGE,"E4.bottom"),sQuery(id+"F0.wireOp",EDGE,"E4.right")])]});
            var Q1;
            Q1=makeQuery(id+"F1.opExtrude","SWEPT_EDGE",EDGE,{"disambiguationData":[OSD([sQuery(id+"F0.wireOp",EDGE,"E6.bottom"),sQuery(id+"F0.wireOp",EDGE,"E6.right")])]});
            var Q2;
            Q2=makeQuery(id+"F1.opExtrude","SWEPT_EDGE",EDGE,{"disambiguationData":[OSD([sQuery(id+"F0.wireOp",EDGE,"E4.bottom"),sQuery(id+"F0.wireOp",EDGE,"E4.left")])]});
            var Q3;
            Q3=makeQuery(id+"F1.opExtrude","SWEPT_EDGE",EDGE,{"disambiguationData":[OSD([sQuery(id+"F0.wireOp",EDGE,"E6.bottom"),sQuery(id+"F0.wireOp",EDGE,"E6.left")])]});
            var Q4;
            Q4=makeQuery(id+"F1.opExtrude","SWEPT_EDGE",EDGE,{"disambiguationData":[OSD([sQuery(id+"F0.wireOp",EDGE,"E6.top"),sQuery(id+"F0.wireOp",EDGE,"E6.left")])]});
            var Q5;
            Q5=makeQuery(id+"F1.opExtrude","SWEPT_EDGE",EDGE,{"disambiguationData":[OSD([sQuery(id+"F0.wireOp",EDGE,"E4.top"),sQuery(id+"F0.wireOp",EDGE,"E4.left")])]});
            var Q6;
            Q6=makeQuery(id+"F1.opExtrude","SWEPT_EDGE",EDGE,{"disambiguationData":[OSD([sQuery(id+"F0.wireOp",EDGE,"E6.top"),sQuery(id+"F0.wireOp",EDGE,"E6.right")])]});
            var Q7;
            Q7=makeQuery(id+"F1.opExtrude","SWEPT_EDGE",EDGE,{"disambiguationData":[OSD([sQuery(id+"F0.wireOp",EDGE,"E4.top"),sQuery(id+"F0.wireOp",EDGE,"E4.right")])]});
            var Q8;
            Q8=makeQuery(id+"F1.opExtrude","CAP_EDGE",EDGE,{"disambiguationData":[OSD([sQuery(id+"F0.wireOp",EDGE,"E4.top")])],"isStart":true});
            var Q9;
            Q9=makeQuery(id+"F1.opExtrude","CAP_EDGE",EDGE,{"disambiguationData":[OSD([sQuery(id+"F0.wireOp",EDGE,"E6.bottom")])],"isStart":true});
            var Q10;
            Q10=makeQuery(id+"F1.opExtrude","CAP_EDGE",EDGE,{"disambiguationData":[OSD([sQuery(id+"F0.wireOp",EDGE,"E4.bottom")])],"isStart":false});
            var Q11;
            Q11=makeQuery(id+"F1.opExtrude","CAP_EDGE",EDGE,{"disambiguationData":[OSD([sQuery(id+"F0.wireOp",EDGE,"E6.bottom")])],"isStart":false});
            var Q12;
            Q12=makeQuery(id+"F17.boolean.opBoolean","COPY",EDGE,{"derivedFrom":makeQuery(id+"F17.opExtrude","CAP_EDGE",EDGE,{"disambiguationData":[OSD([sQuery(id+"F11.wireOp",EDGE,"E19")])],"isStart":false})});
            var Q13;
            Q13=makeQuery(id+"F17.boolean.opBoolean","COPY",EDGE,{"disambiguationData":[OD(1.0)],"derivedFrom":makeQuery(id+"F17.opExtrude","CAP_EDGE",EDGE,{"disambiguationData":[OSD([sQuery(id+"F11.wireOp",EDGE,"E20")])],"isStart":false})});
            var Q14;
            Q14=makeQuery(id+"F17.boolean.opBoolean","COPY",EDGE,{"disambiguationData":[OD(2.0)],"derivedFrom":makeQuery(id+"F17.opExtrude","CAP_EDGE",EDGE,{"disambiguationData":[OSD([sQuery(id+"F11.wireOp",EDGE,"E20")])],"isStart":false})});
            var Q15;
            Q15=makeQuery(id+"F17.boolean.opBoolean","COPY",EDGE,{"disambiguationData":[OD(0.0)],"derivedFrom":makeQuery(id+"F17.opExtrude","CAP_EDGE",EDGE,{"disambiguationData":[OSD([sQuery(id+"F11.wireOp",EDGE,"E20")])],"isStart":false})});
            var Q16;
            {var subQ0=sQuery(id+"F11.wireOp",EDGE,"E23");var subQ1=sQuery(id+"F11.wireOp",EDGE,"E19");Q16=qUnion([makeQuery(id+"F14.boolean.opBoolean","COPY",EDGE,{"derivedFrom":makeQuery(id+"F14.opExtrude","CAP_EDGE",EDGE,{"disambiguationData":[OSD([subQ1]),TDD([makeQuery(id+"F11.imprint","IMPRINT",EDGE,{"disambiguationData":[TD([[makeQuery(id+"F11.imprint","INTERSECT",VERTEX,{"disambiguationData":[OD(0.0)],"derivedFrom":[subQ1,subQ0]}),-1.0]])],"derivedFrom":subQ1})])],"isStart":false})}),makeQuery(id+"F14.boolean.opBoolean","COPY",EDGE,{"derivedFrom":makeQuery(id+"F14.opExtrude","CAP_EDGE",EDGE,{"disambiguationData":[OSD([subQ1]),TDD([makeQuery(id+"F11.imprint","IMPRINT",EDGE,{"disambiguationData":[TD([[makeQuery(id+"F11.imprint","INTERSECT",VERTEX,{"disambiguationData":[OD(1.0)],"derivedFrom":[subQ1,subQ0]}),1.0]])],"derivedFrom":subQ1})])],"isStart":false})})]);}
            var Q17;
            Q17=makeQuery(id+"F13.opExtrude","CAP_EDGE",EDGE,{"disambiguationData":[OSD([sQuery(id+"F9.wireOp",EDGE,"E18.top")])],"isStart":false});
            fillet(context, id + "F19", {"entities" : qUnion([Q0, Q1, Q2, Q3, Q4, Q5, Q6, Q7, Q8, Q9, Q10, Q11, Q12, Q13, Q14, Q15, Q16, Q17]), "radius" : 0.38 * mm, "tangentPropagation" : true, "allowEdgeOverflow" : false});
        }
        {
            var Q0;
            {var subQ0=sQuery(id+"F0.wireOp",EDGE,"E1.top");var subQ1=sQuery(id+"F0.wireOp",EDGE,"E1.bottom");Q0=makeQuery(id+"F17.boolean.opBoolean","INTERSECT",EDGE,{"derivedFrom":[makeQuery(id+"F6.boolean.opBoolean","MERGE",FACE,{"derivedFrom":[makeQuery(id+"F5.boolean.opBoolean","MERGE",FACE,{"derivedFrom":[makeQuery(id+"F1.opExtrude","CAP_FACE",FACE,{"disambiguationData":[OSD([subQ1,subQ0,sQuery(id+"F0.wireOp",EDGE,"E1.left"),sQuery(id+"F0.wireOp",EDGE,"E1.right"),sQuery(id+"F0.wireOp",EDGE,"E4.bottom"),sQuery(id+"F0.wireOp",EDGE,"E4.top"),sQuery(id+"F0.wireOp",EDGE,"E4.left"),sQuery(id+"F0.wireOp",EDGE,"E4.right"),sQuery(id+"F0.wireOp",EDGE,"E6.bottom"),sQuery(id+"F0.wireOp",EDGE,"E6.top"),sQuery(id+"F0.wireOp",EDGE,"E6.left"),sQuery(id+"F0.wireOp",EDGE,"E6.right")])],"isStart":true}),makeQuery(id+"F5.opExtrude","SWEPT_FACE",FACE,{"disambiguationData":[OSD([subQ1]),TDD([makeQuery(id+"F1.opExtrude","CAP_EDGE",EDGE,{"disambiguationData":[OSD([subQ1])],"isStart":true})])]})]}),makeQuery(id+"F6.opExtrude","SWEPT_FACE",FACE,{"disambiguationData":[OSD([subQ0]),TDD([makeQuery(id+"F1.opExtrude","CAP_EDGE",EDGE,{"disambiguationData":[OSD([subQ0])],"isStart":true})])]})]}),makeQuery(id+"F17.opExtrude","CAP_FACE",FACE,{"disambiguationData":[OSD([sQuery(id+"F11.wireOp",EDGE,"E19"),sQuery(id+"F11.wireOp",EDGE,"E20")])],"isStart":false})]});}
            fillet(context, id + "F20", {"entities" : qUnion([Q0]), "radius" : 0.38 * mm, "tangentPropagation" : true, "allowEdgeOverflow" : false});
        }
        {
            var Q0;
            {var subQ0=sQuery(id+"F0.wireOp",EDGE,"E1.top");var subQ1=sQuery(id+"F0.wireOp",EDGE,"E1.bottom");Q0=makeQuery(id+"F16.opFillet","SPLIT",FACE,{"disambiguationData":[OD(1.0)],"derivedFrom":makeQuery(id+"F6.boolean.opBoolean","MERGE",FACE,{"derivedFrom":[makeQuery(id+"F5.boolean.opBoolean","MERGE",FACE,{"derivedFrom":[makeQuery(id+"F4.boolean.opBoolean","MERGE",FACE,{"derivedFrom":[makeQuery(id+"F2.opExtrude","CAP_FACE",FACE,{"disambiguationData":[OSD([sQuery(id+"F0.wireOp",EDGE,"E0.bottom"),sQuery(id+"F0.wireOp",EDGE,"E0.top"),sQuery(id+"F0.wireOp",EDGE,"E0.left"),sQuery(id+"F0.wireOp",EDGE,"E0.right"),subQ1,subQ0,sQuery(id+"F0.wireOp",EDGE,"E1.left"),sQuery(id+"F0.wireOp",EDGE,"E1.right")])],"isStart":false}),makeQuery(id+"F4.opExtrude","CAP_FACE",FACE,{"disambiguationData":[OSD([sQuery(id+"F3.wireOp",EDGE,"E7"),sQuery(id+"F3.wireOp",EDGE,"E10")])],"isStart":true}),makeQuery(id+"F4.opExtrude","CAP_FACE",FACE,{"disambiguationData":[OSD([sQuery(id+"F3.wireOp",EDGE,"E8"),sQuery(id+"F3.wireOp",EDGE,"E9")])],"isStart":true})]}),makeQuery(id+"F5.opExtrude","SWEPT_FACE",FACE,{"disambiguationData":[OSD([subQ1]),TDD([makeQuery(id+"F2.opExtrude","CAP_EDGE",EDGE,{"disambiguationData":[OSD([subQ1])],"isStart":false})])]})]}),makeQuery(id+"F6.opExtrude","SWEPT_FACE",FACE,{"disambiguationData":[OSD([subQ0]),TDD([makeQuery(id+"F2.opExtrude","CAP_EDGE",EDGE,{"disambiguationData":[OSD([subQ0])],"isStart":false})])]})]})});}
            var sketch = newSketch(context, id + "F21", { "sketchPlane" : qUnion([Q0])});
            skLineSegment(sketch, "E25.bottom", {"start": v(8, -30.48) * mm, "end": v(-8, -30.48) * mm});
            skLineSegment(sketch, "E25.top", {"start": v(8, 30.48) * mm, "end": v(-8, 30.48) * mm});
            skLineSegment(sketch, "E25.left", {"start": v(8, -30.48) * mm, "end": v(8, 30.48) * mm});
            skLineSegment(sketch, "E25.right", {"start": v(-8, -30.48) * mm, "end": v(-8, 30.48) * mm});
            skPoint(sketch, "E25.middle", {"position": v(0, 0) * mm});
            skSolve(sketch);
        }
        {
            var Q0;
            Q0 = qSketchRegion(id + "F21", true);
            extrude(context, id + "F22", {"entities" : qUnion([Q0]), "operationType" : NewBodyOperationType.REMOVE, "oppositeDirection" : true, "depth" : 1.52 * mm});
        }
        {
            var Q0;
            {var subQ0=sQuery(id+"F11.wireOp",EDGE,"E19");Q0=makeQuery(id+"F17.boolean.opBoolean","INTERSECT",EDGE,{"derivedFrom":[makeQuery(id+"F14.boolean.opBoolean","COPY",FACE,{"derivedFrom":makeQuery(id+"F14.opExtrude","SWEPT_FACE",FACE,{"disambiguationData":[OSD([subQ0]),TDD([makeQuery(id+"F11.imprint","IMPRINT",EDGE,{"disambiguationData":[TD([[makeQuery(id+"F11.imprint","INTERSECT",VERTEX,{"disambiguationData":[OD(1.0)],"derivedFrom":[subQ0,sQuery(id+"F11.wireOp",EDGE,"E23")]}),1.0]])],"derivedFrom":subQ0})])]})}),makeQuery(id+"F17.opExtrude","CAP_FACE",FACE,{"disambiguationData":[OSD([sQuery(id+"F11.wireOp",EDGE,"E20")])],"isStart":false})]});}
            var Q1;
            Q1=makeQuery(id+"F17.boolean.opBoolean","INTERSECT",EDGE,{"derivedFrom":[makeQuery(id+"F14.boolean.opBoolean","COPY",FACE,{"derivedFrom":makeQuery(id+"F14.opExtrude","SWEPT_FACE",FACE,{"disambiguationData":[OSD([sQuery(id+"F11.wireOp",EDGE,"E23")])]})}),makeQuery(id+"F17.opExtrude","CAP_FACE",FACE,{"disambiguationData":[OSD([sQuery(id+"F11.wireOp",EDGE,"E20")])],"isStart":false})]});
            var Q2;
            {var subQ0=sQuery(id+"F11.wireOp",EDGE,"E19");Q2=makeQuery(id+"F17.boolean.opBoolean","INTERSECT",EDGE,{"derivedFrom":[makeQuery(id+"F14.boolean.opBoolean","COPY",FACE,{"derivedFrom":makeQuery(id+"F14.opExtrude","SWEPT_FACE",FACE,{"disambiguationData":[OSD([subQ0]),TDD([makeQuery(id+"F11.imprint","IMPRINT",EDGE,{"disambiguationData":[TD([[makeQuery(id+"F11.imprint","INTERSECT",VERTEX,{"disambiguationData":[OD(0.0)],"derivedFrom":[subQ0,sQuery(id+"F11.wireOp",EDGE,"E23")]}),-1.0]])],"derivedFrom":subQ0})])]})}),makeQuery(id+"F17.opExtrude","CAP_FACE",FACE,{"disambiguationData":[OSD([sQuery(id+"F11.wireOp",EDGE,"E20")])],"isStart":false})]});}
            var Q3;
            Q3=makeQuery(id+"F17.boolean.opBoolean","INTERSECT",EDGE,{"derivedFrom":[makeQuery(id+"F14.boolean.opBoolean","COPY",FACE,{"derivedFrom":makeQuery(id+"F14.opExtrude","SWEPT_FACE",FACE,{"disambiguationData":[OSD([sQuery(id+"F11.wireOp",EDGE,"E21")])]})}),makeQuery(id+"F17.opExtrude","CAP_FACE",FACE,{"disambiguationData":[OSD([sQuery(id+"F11.wireOp",EDGE,"E20")])],"isStart":false})]});
            var Q4;
            Q4=makeQuery(id+"F14.boolean.opBoolean","COPY",EDGE,{"derivedFrom":makeQuery(id+"F14.opExtrude","CAP_EDGE",EDGE,{"disambiguationData":[OSD([sQuery(id+"F11.wireOp",EDGE,"E23")])],"isStart":false})});
            var Q5;
            Q5=makeQuery(id+"F14.boolean.opBoolean","COPY",EDGE,{"derivedFrom":makeQuery(id+"F14.opExtrude","CAP_EDGE",EDGE,{"disambiguationData":[OSD([sQuery(id+"F11.wireOp",EDGE,"E21")])],"isStart":false})});
            fillet(context, id + "F23", {"entities" : qUnion([Q0, Q1, Q2, Q3, Q4, Q5]), "radius" : 0.38 * mm, "tangentPropagation" : true, "allowEdgeOverflow" : false});
        }
        {
            var Q0;
            Q0=qCreatedBy(makeId("Front.planeOp"),FACE);
            cPlane(context, id + "F24", {"entities" : qUnion([Q0]), "cplaneType" : CPlaneType.OFFSET, "offset" : 38.1 * mm, "width" : 152.4 * mm, "height" : 152.4 * mm});
        }
        {
            var Q0;
            Q0=qCreatedBy(id+"F24.planeOp",FACE);
            var sketch = newSketch(context, id + "F25", { "sketchPlane" : qUnion([Q0])});
            skCircle(sketch, "E26", {"center": v(6.03, 4) * mm, "radius": 1.97 * mm});
            skLineSegment(sketch, "E27.bottom", {"start": v(4.15, 4.58) * mm, "end": v(1.61, 4.58) * mm});
            skLineSegment(sketch, "E27.top", {"start": v(4.15, 3.42) * mm, "end": v(1.61, 3.42) * mm});
            skLineSegment(sketch, "E27.left", {"start": v(4.15, 4.58) * mm, "end": v(4.15, 3.42) * mm});
            skLineSegment(sketch, "E27.right", {"start": v(1.61, 4.58) * mm, "end": v(1.61, 3.42) * mm});
            skPoint(sketch, "E27.middle", {"position": v(2.88, 4) * mm});
            skSolve(sketch);
        }
        {
            var Q0;
            {var subQ0=sQuery(id+"F25.wireOp",EDGE,"E27.left");Q0=makeQuery(id+"F25.imprint","IMPRINT",FACE,{"disambiguationData":[TD([[makeQuery(id+"F25.imprint","IMPRINT",EDGE,{"derivedFrom":subQ0}),1.0]])]});}
            var Q1;
            {var subQ0=sQuery(id+"F25.wireOp",EDGE,"E27.left");Q1=makeQuery(id+"F25.imprint","IMPRINT",FACE,{"disambiguationData":[TD([[makeQuery(id+"F25.imprint","IMPRINT",EDGE,{"derivedFrom":subQ0}),-1.0]])]});}
            extrude(context, id + "F26", {"entities" : qUnion([Q0, Q1]), "operationType" : NewBodyOperationType.REMOVE, "oppositeDirection" : true, "depth" : 25.4 * mm});
        }
        {
            var Q0;
            Q0=makeQuery(id+"F22.boolean.opBoolean","INTERSECT",EDGE,{"derivedFrom":[makeQuery(id+"F4.opExtrude","SWEPT_FACE",FACE,{"disambiguationData":[OSD([sQuery(id+"F3.wireOp",EDGE,"E9")])]}),makeQuery(id+"F22.opExtrude","CAP_FACE",FACE,{"disambiguationData":[OSD([sQuery(id+"F21.wireOp",EDGE,"E25.bottom"),sQuery(id+"F21.wireOp",EDGE,"E25.top"),sQuery(id+"F21.wireOp",EDGE,"E25.left"),sQuery(id+"F21.wireOp",EDGE,"E25.right")])],"isStart":false})]});
            var Q1;
            Q1=makeQuery(id+"F22.boolean.opBoolean","INTERSECT",EDGE,{"derivedFrom":[makeQuery(id+"F4.opExtrude","SWEPT_FACE",FACE,{"disambiguationData":[OSD([sQuery(id+"F3.wireOp",EDGE,"E10")])]}),makeQuery(id+"F22.opExtrude","CAP_FACE",FACE,{"disambiguationData":[OSD([sQuery(id+"F21.wireOp",EDGE,"E25.bottom"),sQuery(id+"F21.wireOp",EDGE,"E25.top"),sQuery(id+"F21.wireOp",EDGE,"E25.left"),sQuery(id+"F21.wireOp",EDGE,"E25.right")])],"isStart":false})]});
            chamfer(context, id + "F27", {"entities" : qUnion([Q0, Q1]), "width" : 0.25 * mm, "tangentPropagation" : true});
        }
        {
            var Q0;
            Q0=makeQuery(id+"F22.boolean.opBoolean","INTERSECT",EDGE,{"derivedFrom":[makeQuery(id+"F4.opExtrude","SWEPT_FACE",FACE,{"disambiguationData":[OSD([sQuery(id+"F3.wireOp",EDGE,"E7")])]}),makeQuery(id+"F22.opExtrude","CAP_FACE",FACE,{"disambiguationData":[OSD([sQuery(id+"F21.wireOp",EDGE,"E25.bottom"),sQuery(id+"F21.wireOp",EDGE,"E25.top"),sQuery(id+"F21.wireOp",EDGE,"E25.left"),sQuery(id+"F21.wireOp",EDGE,"E25.right")])],"isStart":false})]});
            var Q1;
            Q1=makeQuery(id+"F22.boolean.opBoolean","INTERSECT",EDGE,{"derivedFrom":[makeQuery(id+"F4.opExtrude","SWEPT_FACE",FACE,{"disambiguationData":[OSD([sQuery(id+"F3.wireOp",EDGE,"E8")])]}),makeQuery(id+"F22.opExtrude","CAP_FACE",FACE,{"disambiguationData":[OSD([sQuery(id+"F21.wireOp",EDGE,"E25.bottom"),sQuery(id+"F21.wireOp",EDGE,"E25.top"),sQuery(id+"F21.wireOp",EDGE,"E25.left"),sQuery(id+"F21.wireOp",EDGE,"E25.right")])],"isStart":false})]});
            var Q2;
            {var subQ0=sQuery(id+"F3.wireOp",EDGE,"E8");var subQ1=makeQuery(id+"F2.opExtrude","SWEPT_FACE",FACE,{"disambiguationData":[OSD([sQuery(id+"F0.wireOp",EDGE,"E0.top")])]});Q2=makeQuery(id+"F18.opFillet","BLEND_EDGE",EDGE,{"blendedFrom":[makeQuery(id+"F4.boolean.opBoolean","INTERSECT",EDGE,{"disambiguationData":[OD(0.0)],"derivedFrom":[subQ1,makeQuery(id+"F4.opExtrude","SWEPT_FACE",FACE,{"disambiguationData":[OSD([subQ0])]})]}),makeQuery(id+"F4.boolean.opBoolean","INTERSECT",EDGE,{"disambiguationData":[OD(0.0)],"derivedFrom":[subQ1,makeQuery(id+"F4.opExtrude","CAP_FACE",FACE,{"disambiguationData":[OSD([subQ0,sQuery(id+"F3.wireOp",EDGE,"E9")])],"isStart":false})]})],"blendedInto":[]});}
            var Q3;
            {var subQ0=sQuery(id+"F3.wireOp",EDGE,"E7");var subQ1=makeQuery(id+"F2.opExtrude","SWEPT_FACE",FACE,{"disambiguationData":[OSD([sQuery(id+"F0.wireOp",EDGE,"E0.bottom")])]});Q3=makeQuery(id+"F18.opFillet","BLEND_EDGE",EDGE,{"blendedFrom":[makeQuery(id+"F4.boolean.opBoolean","INTERSECT",EDGE,{"disambiguationData":[OD(0.0)],"derivedFrom":[subQ1,makeQuery(id+"F4.opExtrude","SWEPT_FACE",FACE,{"disambiguationData":[OSD([subQ0])]})]}),makeQuery(id+"F4.boolean.opBoolean","INTERSECT",EDGE,{"disambiguationData":[OD(0.0)],"derivedFrom":[subQ1,makeQuery(id+"F4.opExtrude","CAP_FACE",FACE,{"disambiguationData":[OSD([subQ0,sQuery(id+"F3.wireOp",EDGE,"E10")])],"isStart":false})]})],"blendedInto":[]});}
            fillet(context, id + "F28", {"entities" : qUnion([Q0, Q1, Q2, Q3]), "radius" : 0.25 * mm, "tangentPropagation" : true, "allowEdgeOverflow" : false});
        }
        {
            var Q0;
            Q0=makeQuery(id+"F22.boolean.opBoolean","COPY",EDGE,{"derivedFrom":makeQuery(id+"F22.opExtrude","CAP_EDGE",EDGE,{"disambiguationData":[OSD([sQuery(id+"F21.wireOp",EDGE,"E25.top")])],"isStart":false})});
            var Q1;
            Q1=makeQuery(id+"F22.boolean.opBoolean","COPY",EDGE,{"derivedFrom":makeQuery(id+"F22.opExtrude","CAP_EDGE",EDGE,{"disambiguationData":[OSD([sQuery(id+"F21.wireOp",EDGE,"E25.bottom")])],"isStart":false})});
            var Q2;
            {var subQ2=sQuery(id+"F0.wireOp",EDGE,"E0.left");var subQ3=sQuery(id+"F0.wireOp",EDGE,"E0.right");var subQ4=sQuery(id+"F0.wireOp",EDGE,"E0.bottom");var subQ9=makeQuery(id+"F2.opExtrude","CAP_EDGE",EDGE,{"disambiguationData":[OSD([subQ4])],"isStart":false});Q2=makeQuery(id+"F22.boolean.opBoolean","MERGE",EDGE,{"derivedFrom":[makeQuery(id+"F4.boolean.opBoolean","SPLIT",EDGE,{"disambiguationData":[TD([makeQuery(id+"F2.opExtrude","SWEPT_FACE",FACE,{"disambiguationData":[OSD([subQ3])]})])],"derivedFrom":subQ9}),makeQuery(id+"F4.boolean.opBoolean","SPLIT",EDGE,{"disambiguationData":[TD([makeQuery(id+"F2.opExtrude","SWEPT_FACE",FACE,{"disambiguationData":[OSD([subQ2])]})])],"derivedFrom":subQ9}),makeQuery(id+"F22.opExtrude","CAP_EDGE",EDGE,{"disambiguationData":[OSD([sQuery(id+"F21.wireOp",EDGE,"E25.top")])],"isStart":true})]});}
            fillet(context, id + "F29", {"entities" : qUnion([Q0, Q1, Q2]), "radius" : 0.25 * mm, "tangentPropagation" : true, "allowEdgeOverflow" : false});
        }
        {
            var Q0;
            {var subQ0=sQuery(id+"F0.wireOp",EDGE,"E1.top");var subQ1=sQuery(id+"F0.wireOp",EDGE,"E1.bottom");Q0=makeQuery(id+"F6.boolean.opBoolean","MERGE",FACE,{"derivedFrom":[makeQuery(id+"F5.boolean.opBoolean","MERGE",FACE,{"derivedFrom":[makeQuery(id+"F1.opExtrude","CAP_FACE",FACE,{"disambiguationData":[OSD([subQ1,subQ0,sQuery(id+"F0.wireOp",EDGE,"E1.left"),sQuery(id+"F0.wireOp",EDGE,"E1.right"),sQuery(id+"F0.wireOp",EDGE,"E4.bottom"),sQuery(id+"F0.wireOp",EDGE,"E4.top"),sQuery(id+"F0.wireOp",EDGE,"E4.left"),sQuery(id+"F0.wireOp",EDGE,"E4.right"),sQuery(id+"F0.wireOp",EDGE,"E6.bottom"),sQuery(id+"F0.wireOp",EDGE,"E6.top"),sQuery(id+"F0.wireOp",EDGE,"E6.left"),sQuery(id+"F0.wireOp",EDGE,"E6.right")])],"isStart":true}),makeQuery(id+"F5.opExtrude","SWEPT_FACE",FACE,{"disambiguationData":[OSD([subQ1]),TDD([makeQuery(id+"F1.opExtrude","CAP_EDGE",EDGE,{"disambiguationData":[OSD([subQ1])],"isStart":true})])]})]}),makeQuery(id+"F6.opExtrude","SWEPT_FACE",FACE,{"disambiguationData":[OSD([subQ0]),TDD([makeQuery(id+"F1.opExtrude","CAP_EDGE",EDGE,{"disambiguationData":[OSD([subQ0])],"isStart":true})])]})]});}
            var sketch = newSketch(context, id + "F30", { "sketchPlane" : qUnion([Q0])});
            skText(sketch, "E28", { "text": "Power\n", "fontName": "OpenSans-Bold.ttf"});
            skText(sketch, "E29", { "text": "Lights\n", "fontName": "OpenSans-Bold.ttf"});
            skText(sketch, "E30", { "text": "2S Only", "fontName": "OpenSans-Bold.ttf"});
            const initialGuessF30  = {"E28": [-0.00737, 0.02536, 1, 0, 0.00332], "E29": [-0.00737, -0.0119, 1, 0, 0.00348], "E30": [-0.00737, -0.02509, 1, 0, 0.00281]};
            skSetInitialGuess(sketch, initialGuessF30);
            skSolve(sketch);
        }
        {
            var Q0;
            Q0 = qSketchRegion(id + "F30", true);
            extrude(context, id + "F31", {"entities" : qUnion([Q0]), "operationType" : NewBodyOperationType.REMOVE, "oppositeDirection" : true, "depth" : 0.5 * mm});
        }
        {
            var Q0;
            {var subQ2=sQuery(id+"F0.wireOp",EDGE,"E0.top");var subQ3=makeQuery(id+"F2.opExtrude","SWEPT_FACE",FACE,{"disambiguationData":[OSD([subQ2])]});var subQ15=sQuery(id+"F0.wireOp",EDGE,"E1.bottom");var subQ18=sQuery(id+"F21.wireOp",EDGE,"E25.bottom");Q0=makeQuery(id+"F26.boolean.opBoolean","SPLIT",FACE,{"disambiguationData":[TD([makeQuery(id+"F5.opExtrude","SWEPT_FACE",FACE,{"disambiguationData":[OSD([subQ15]),TDD([makeQuery(id+"F2.opExtrude","CAP_EDGE",EDGE,{"disambiguationData":[OSD([subQ15])],"isStart":false})])]})])],"derivedFrom":makeQuery(id+"F22.boolean.opBoolean","MERGE",FACE,{"derivedFrom":[subQ3,makeQuery(id+"F22.opExtrude","SWEPT_FACE",FACE,{"disambiguationData":[OSD([subQ18])]})]})});}
            var sketch = newSketch(context, id + "F32", { "sketchPlane" : qUnion([Q0])});
            skLineSegment(sketch, "E31.bottom", {"start": v(-4.2, 7.11) * mm, "end": v(4.2, 7.11) * mm});
            skLineSegment(sketch, "E31.top", {"start": v(-4.2, 0) * mm, "end": v(4.2, 0) * mm});
            skLineSegment(sketch, "E31.left", {"start": v(-4.2, 7.11) * mm, "end": v(-4.2, 0) * mm});
            skLineSegment(sketch, "E31.right", {"start": v(4.2, 7.11) * mm, "end": v(4.2, 0) * mm});
            skPoint(sketch, "E31.middle", {"position": v(0, 3.56) * mm});
            skSolve(sketch);
        }
        {
            var Q0;
            {var subQ33=sQuery(id+"F32.wireOp",EDGE,"E31.bottom");Q0=makeQuery(id+"F32.imprint","IMPRINT",FACE,{"disambiguationData":[TD([[makeQuery(id+"F32.imprint","IMPRINT",EDGE,{"derivedFrom":subQ33}),-1.0]])]});}
            extrude(context, id + "F33", {"entities" : qUnion([Q0]), "operationType" : NewBodyOperationType.ADD, "depth" : 3.8 * mm});
        }
        {
            var Q0;
            Q0=qCreatedBy(id+"F24.planeOp",FACE);
            var sketch = newSketch(context, id + "F34", { "sketchPlane" : qUnion([Q0])});
            skLineSegment(sketch, "E32.bottom", {"start": v(3.04, 6.83) * mm, "end": v(-3.04, 6.83) * mm});
            skLineSegment(sketch, "E32.top", {"start": v(3.04, 2.03) * mm, "end": v(-3.04, 2.03) * mm});
            skLineSegment(sketch, "E32.left", {"start": v(3.04, 6.83) * mm, "end": v(3.04, 2.03) * mm});
            skLineSegment(sketch, "E32.right", {"start": v(-3.04, 6.83) * mm, "end": v(-3.04, 2.03) * mm});
            skPoint(sketch, "E32.middle", {"position": v(0, 4.43) * mm});
            skLineSegment(sketch, "E33.bottom", {"start": v(2.02, 5.3) * mm, "end": v(-2.02, 5.3) * mm});
            skLineSegment(sketch, "E33.top", {"start": v(2.02, 2.54) * mm, "end": v(-2.02, 2.54) * mm});
            skLineSegment(sketch, "E33.left", {"start": v(2.02, 5.3) * mm, "end": v(2.02, 2.54) * mm});
            skLineSegment(sketch, "E33.right", {"start": v(-2.02, 5.3) * mm, "end": v(-2.02, 2.54) * mm});
            skPoint(sketch, "E33.middle", {"position": v(0, 3.92) * mm});
            skPoint(sketch, "E33.middle.positionSnap0", {"position": v(0, 2.03) * mm});
            skPoint(sketch, "E33.centerSnap0", {"position": v(0, 2.03) * mm});
            skSolve(sketch);
        }
        {
            var Q0;
            Q0=makeQuery(id+"F34.imprint","IMPRINT",FACE,{"disambiguationData":[TD([[makeQuery(id+"F34.imprint","IMPRINT",EDGE,{"derivedFrom":sQuery(id+"F34.wireOp",EDGE,"E33.bottom")}),1.0]])]});
            var Q1;
            Q1=makeQuery(id+"F34.imprint","IMPRINT",FACE,{"disambiguationData":[TD([[makeQuery(id+"F34.imprint","IMPRINT",EDGE,{"derivedFrom":sQuery(id+"F34.wireOp",EDGE,"E32.bottom")}),1.0]])]});
            extrude(context, id + "F35", {"entities" : qUnion([Q0, Q1]), "operationType" : NewBodyOperationType.REMOVE, "oppositeDirection" : true, "depth" : 10.54 * mm});
        }
        {
            var Q0;
            Q0=makeQuery(id+"F33.opExtrude","CAP_EDGE",EDGE,{"disambiguationData":[OSD([sQuery(id+"F32.wireOp",EDGE,"E31.bottom")])],"isStart":true});
            var Q1;
            Q1=makeQuery(id+"F33.opExtrude","CAP_EDGE",EDGE,{"disambiguationData":[OSD([sQuery(id+"F32.wireOp",EDGE,"E31.left")])],"isStart":true});
            var Q2;
            Q2=makeQuery(id+"F33.opExtrude","CAP_EDGE",EDGE,{"disambiguationData":[OSD([sQuery(id+"F32.wireOp",EDGE,"E31.right")])],"isStart":true});
            var Q3;
            Q3=makeQuery(id+"F33.opExtrude","CAP_EDGE",EDGE,{"disambiguationData":[OSD([sQuery(id+"F32.wireOp",EDGE,"E31.top")])],"isStart":true});
            fillet(context, id + "F36", {"entities" : qUnion([Q0, Q1, Q2, Q3]), "radius" : 0.5 * mm, "tangentPropagation" : true, "allowEdgeOverflow" : false});
        }
        {
            var Q0;
            Q0=makeQuery(id+"F34.imprint","IMPRINT",FACE,{"disambiguationData":[TD([[makeQuery(id+"F34.imprint","IMPRINT",EDGE,{"derivedFrom":sQuery(id+"F34.wireOp",EDGE,"E33.bottom")}),1.0]])]});
            extrude(context, id + "F37", {"entities" : qUnion([Q0]), "operationType" : NewBodyOperationType.REMOVE, "oppositeDirection" : true, "depth" : 25.4 * mm});
        }
        {
            var Q0;
            Q0=makeQuery(id+"F2.boolean.opBoolean","INTERSECT",EDGE,{"derivedFrom":[makeQuery(id+"F1.opExtrude","CAP_FACE",FACE,{"disambiguationData":[OSD([sQuery(id+"F0.wireOp",EDGE,"E1.bottom"),sQuery(id+"F0.wireOp",EDGE,"E1.top"),sQuery(id+"F0.wireOp",EDGE,"E1.left"),sQuery(id+"F0.wireOp",EDGE,"E1.right"),sQuery(id+"F0.wireOp",EDGE,"E4.bottom"),sQuery(id+"F0.wireOp",EDGE,"E4.top"),sQuery(id+"F0.wireOp",EDGE,"E4.left"),sQuery(id+"F0.wireOp",EDGE,"E4.right"),sQuery(id+"F0.wireOp",EDGE,"E6.bottom"),sQuery(id+"F0.wireOp",EDGE,"E6.top"),sQuery(id+"F0.wireOp",EDGE,"E6.left"),sQuery(id+"F0.wireOp",EDGE,"E6.right")])],"isStart":false}),makeQuery(id+"F2.opExtrude","SWEPT_FACE",FACE,{"disambiguationData":[OSD([sQuery(id+"F0.wireOp",EDGE,"E0.left")])]})]});
            var Q1;
            Q1=makeQuery(id+"F2.boolean.opBoolean","INTERSECT",EDGE,{"derivedFrom":[makeQuery(id+"F1.opExtrude","CAP_FACE",FACE,{"disambiguationData":[OSD([sQuery(id+"F0.wireOp",EDGE,"E1.bottom"),sQuery(id+"F0.wireOp",EDGE,"E1.top"),sQuery(id+"F0.wireOp",EDGE,"E1.left"),sQuery(id+"F0.wireOp",EDGE,"E1.right"),sQuery(id+"F0.wireOp",EDGE,"E4.bottom"),sQuery(id+"F0.wireOp",EDGE,"E4.top"),sQuery(id+"F0.wireOp",EDGE,"E4.left"),sQuery(id+"F0.wireOp",EDGE,"E4.right"),sQuery(id+"F0.wireOp",EDGE,"E6.bottom"),sQuery(id+"F0.wireOp",EDGE,"E6.top"),sQuery(id+"F0.wireOp",EDGE,"E6.left"),sQuery(id+"F0.wireOp",EDGE,"E6.right")])],"isStart":false}),makeQuery(id+"F2.opExtrude","SWEPT_FACE",FACE,{"disambiguationData":[OSD([sQuery(id+"F0.wireOp",EDGE,"E0.right")])]})]});
            var Q2;
            Q2=makeQuery(id+"F2.opExtrude","SWEPT_EDGE",EDGE,{"disambiguationData":[OSD([sQuery(id+"F0.wireOp",EDGE,"E0.top"),sQuery(id+"F0.wireOp",EDGE,"E0.right")])]});
            var Q3;
            Q3=makeQuery(id+"F2.opExtrude","SWEPT_EDGE",EDGE,{"disambiguationData":[OSD([sQuery(id+"F0.wireOp",EDGE,"E0.top"),sQuery(id+"F0.wireOp",EDGE,"E0.left")])]});
            var Q4;
            Q4=makeQuery(id+"F2.opExtrude","SWEPT_EDGE",EDGE,{"disambiguationData":[OSD([sQuery(id+"F0.wireOp",EDGE,"E0.bottom"),sQuery(id+"F0.wireOp",EDGE,"E0.right")])]});
            var Q5;
            Q5=makeQuery(id+"F2.opExtrude","SWEPT_EDGE",EDGE,{"disambiguationData":[OSD([sQuery(id+"F0.wireOp",EDGE,"E0.bottom"),sQuery(id+"F0.wireOp",EDGE,"E0.left")])]});
            var Q6;
            Q6=makeQuery(id+"F2.boolean.opBoolean","INTERSECT",EDGE,{"derivedFrom":[makeQuery(id+"F1.opExtrude","CAP_FACE",FACE,{"disambiguationData":[OSD([sQuery(id+"F0.wireOp",EDGE,"E1.bottom"),sQuery(id+"F0.wireOp",EDGE,"E1.top"),sQuery(id+"F0.wireOp",EDGE,"E1.left"),sQuery(id+"F0.wireOp",EDGE,"E1.right"),sQuery(id+"F0.wireOp",EDGE,"E4.bottom"),sQuery(id+"F0.wireOp",EDGE,"E4.top"),sQuery(id+"F0.wireOp",EDGE,"E4.left"),sQuery(id+"F0.wireOp",EDGE,"E4.right"),sQuery(id+"F0.wireOp",EDGE,"E6.bottom"),sQuery(id+"F0.wireOp",EDGE,"E6.top"),sQuery(id+"F0.wireOp",EDGE,"E6.left"),sQuery(id+"F0.wireOp",EDGE,"E6.right")])],"isStart":false}),makeQuery(id+"F2.opExtrude","SWEPT_FACE",FACE,{"disambiguationData":[OSD([sQuery(id+"F0.wireOp",EDGE,"E0.top")])]})]});
            var Q7;
            Q7=makeQuery(id+"F13.opExtrude","CAP_EDGE",EDGE,{"disambiguationData":[OSD([sQuery(id+"F9.wireOp",EDGE,"E18.top")])],"isStart":true});
            fillet(context, id + "F38", {"entities" : qUnion([Q0, Q1, Q2, Q3, Q4, Q5, Q6, Q7]), "radius" : 0.5 * mm, "tangentPropagation" : true, "allowEdgeOverflow" : false});
        }
        {
            var Q0;
            Q0=makeQuery(id+"F26.boolean.opBoolean","INTERSECT",EDGE,{"derivedFrom":[makeQuery(id+"F15.opFillet","BLEND_FACE",FACE,{"disambiguationData":[OSD([sQuery(id+"F0.wireOp",EDGE,"E1.top"),sQuery(id+"F0.wireOp",EDGE,"E1.left"),sQuery(id+"F7.wireOp",EDGE,"E12.top")])]}),makeQuery(id+"F26.opExtrude","SWEPT_FACE",FACE,{"disambiguationData":[OSD([sQuery(id+"F25.wireOp",EDGE,"E26")])]})]});
            var Q1;
            {var subQ0=sQuery(id+"F25.wireOp",EDGE,"E26");var subQ1=makeQuery(id+"F26.opExtrude","SWEPT_FACE",FACE,{"disambiguationData":[OSD([subQ0])]});var subQ2=sQuery(id+"F21.wireOp",EDGE,"E25.bottom");var subQ3=makeQuery(id+"F22.opExtrude","SWEPT_FACE",FACE,{"disambiguationData":[OSD([subQ2])]});var subQ4=sQuery(id+"F0.wireOp",EDGE,"E0.top");var subQ5=makeQuery(id+"F2.opExtrude","SWEPT_FACE",FACE,{"disambiguationData":[OSD([subQ4])]});var subQ7=makeQuery(id+"F26.boolean.opBoolean","INTERSECT",EDGE,{"disambiguationData":[OD(1.0)],"derivedFrom":[makeQuery(id+"F22.boolean.opBoolean","MERGE",FACE,{"derivedFrom":[subQ5,subQ3]}),subQ1]});Q1=makeQuery(id+"F33.boolean.opBoolean","SPLIT",EDGE,{"disambiguationData":[TD([makeQuery(id+"F2.opExtrude","SWEPT_FACE",FACE,{"disambiguationData":[OSD([sQuery(id+"F0.wireOp",EDGE,"E0.left")])]})])],"derivedFrom":subQ7});}
            var Q2;
            {var subQ0=sQuery(id+"F25.wireOp",EDGE,"E26");var subQ1=sQuery(id+"F21.wireOp",EDGE,"E25.bottom");var subQ2=sQuery(id+"F0.wireOp",EDGE,"E0.top");var subQ3=makeQuery(id+"F26.opExtrude","SWEPT_FACE",FACE,{"disambiguationData":[OSD([subQ0])]});var subQ4=sQuery(id+"F0.wireOp",EDGE,"E0.left");Q2=makeQuery(id+"F38.opFillet","BLEND_EDGE",EDGE,{"blendedFrom":[makeQuery(id+"F26.boolean.opBoolean","SPLIT",EDGE,{"disambiguationData":[TD([makeQuery(id+"F1.opExtrude","CAP_FACE",FACE,{"disambiguationData":[OSD([sQuery(id+"F0.wireOp",EDGE,"E1.bottom"),sQuery(id+"F0.wireOp",EDGE,"E1.top"),sQuery(id+"F0.wireOp",EDGE,"E1.left"),sQuery(id+"F0.wireOp",EDGE,"E1.right"),sQuery(id+"F0.wireOp",EDGE,"E4.bottom"),sQuery(id+"F0.wireOp",EDGE,"E4.top"),sQuery(id+"F0.wireOp",EDGE,"E4.left"),sQuery(id+"F0.wireOp",EDGE,"E4.right"),sQuery(id+"F0.wireOp",EDGE,"E6.bottom"),sQuery(id+"F0.wireOp",EDGE,"E6.top"),sQuery(id+"F0.wireOp",EDGE,"E6.left"),sQuery(id+"F0.wireOp",EDGE,"E6.right")])],"isStart":false})])],"derivedFrom":makeQuery(id+"F2.opExtrude","SWEPT_EDGE",EDGE,{"disambiguationData":[OSD([subQ2,subQ4])]})}),makeQuery(id+"F33.boolean.opBoolean","MERGE",FACE,{"derivedFrom":[makeQuery(id+"F26.boolean.opBoolean","COPY",FACE,{"derivedFrom":subQ3}),makeQuery(id+"F33.opExtrude","SWEPT_FACE",FACE,{"disambiguationData":[OSD([subQ2,subQ1,subQ0])]})]})],"blendedInto":[makeQuery(id+"F33.boolean.opBoolean","MERGE",FACE,{"derivedFrom":[makeQuery(id+"F26.boolean.opBoolean","COPY",FACE,{"derivedFrom":subQ3}),makeQuery(id+"F33.opExtrude","SWEPT_FACE",FACE,{"disambiguationData":[OSD([subQ2,subQ1,subQ0])]})]})]});}
            var Q3;
            {var subQ0=sQuery(id+"F25.wireOp",EDGE,"E26");var subQ1=sQuery(id+"F21.wireOp",EDGE,"E25.bottom");var subQ2=sQuery(id+"F0.wireOp",EDGE,"E0.top");var subQ3=makeQuery(id+"F33.opExtrude","SWEPT_FACE",FACE,{"disambiguationData":[OSD([subQ2,subQ1,subQ0])]});var subQ4=makeQuery(id+"F26.opExtrude","SWEPT_FACE",FACE,{"disambiguationData":[OSD([subQ0])]});var subQ5=makeQuery(id+"F26.boolean.opBoolean","COPY",FACE,{"derivedFrom":subQ4});var subQ7=makeQuery(id+"F2.opExtrude","SWEPT_FACE",FACE,{"disambiguationData":[OSD([subQ2])]});var subQ8=makeQuery(id+"F1.opExtrude","CAP_FACE",FACE,{"disambiguationData":[OSD([sQuery(id+"F0.wireOp",EDGE,"E1.bottom"),sQuery(id+"F0.wireOp",EDGE,"E1.top"),sQuery(id+"F0.wireOp",EDGE,"E1.left"),sQuery(id+"F0.wireOp",EDGE,"E1.right"),sQuery(id+"F0.wireOp",EDGE,"E4.bottom"),sQuery(id+"F0.wireOp",EDGE,"E4.top"),sQuery(id+"F0.wireOp",EDGE,"E4.left"),sQuery(id+"F0.wireOp",EDGE,"E4.right"),sQuery(id+"F0.wireOp",EDGE,"E6.bottom"),sQuery(id+"F0.wireOp",EDGE,"E6.top"),sQuery(id+"F0.wireOp",EDGE,"E6.left"),sQuery(id+"F0.wireOp",EDGE,"E6.right")])],"isStart":false});var subQ10=makeQuery(id+"F26.boolean.opBoolean","SPLIT",EDGE,{"disambiguationData":[TD([makeQuery(id+"F2.opExtrude","SWEPT_FACE",FACE,{"disambiguationData":[OSD([sQuery(id+"F0.wireOp",EDGE,"E0.right")])]})])],"derivedFrom":makeQuery(id+"F2.boolean.opBoolean","INTERSECT",EDGE,{"derivedFrom":[subQ8,subQ7]})});Q3=makeQuery(id+"F38.opFillet","BLEND_EDGE",EDGE,{"blendedFrom":[makeQuery(id+"F33.boolean.opBoolean","SPLIT",EDGE,{"disambiguationData":[TD([subQ5])],"derivedFrom":subQ10}),makeQuery(id+"F33.boolean.opBoolean","MERGE",FACE,{"derivedFrom":[subQ5,subQ3]})],"blendedInto":[makeQuery(id+"F33.boolean.opBoolean","MERGE",FACE,{"derivedFrom":[subQ5,subQ3]})]});}
            fillet(context, id + "F39", {"entities" : qUnion([Q0, Q1, Q2, Q3]), "radius" : 0.5 * mm, "tangentPropagation" : true, "allowEdgeOverflow" : false});
        }
        {
            var Q0;
            Q0=makeQuery(id+"F37.boolean.opBoolean","INTERSECT",EDGE,{"derivedFrom":[makeQuery(id+"F33.opExtrude","CAP_FACE",FACE,{"disambiguationData":[OSD([sQuery(id+"F0.wireOp",EDGE,"E0.top"),sQuery(id+"F0.wireOp",EDGE,"E1.bottom"),sQuery(id+"F0.wireOp",EDGE,"E1.top"),sQuery(id+"F0.wireOp",EDGE,"E1.left"),sQuery(id+"F0.wireOp",EDGE,"E1.right"),sQuery(id+"F0.wireOp",EDGE,"E4.bottom"),sQuery(id+"F0.wireOp",EDGE,"E4.top"),sQuery(id+"F0.wireOp",EDGE,"E4.left"),sQuery(id+"F0.wireOp",EDGE,"E4.right"),sQuery(id+"F0.wireOp",EDGE,"E6.bottom"),sQuery(id+"F0.wireOp",EDGE,"E6.top"),sQuery(id+"F0.wireOp",EDGE,"E6.left"),sQuery(id+"F0.wireOp",EDGE,"E6.right"),sQuery(id+"F21.wireOp",EDGE,"E25.bottom"),sQuery(id+"F25.wireOp",EDGE,"E26"),sQuery(id+"F32.wireOp",EDGE,"E31.bottom"),sQuery(id+"F32.wireOp",EDGE,"E31.left"),sQuery(id+"F32.wireOp",EDGE,"E31.right")])],"isStart":false}),makeQuery(id+"F37.opExtrude","SWEPT_FACE",FACE,{"disambiguationData":[OSD([sQuery(id+"F34.wireOp",EDGE,"E33.right")])]})]});
            var Q1;
            Q1=makeQuery(id+"F37.boolean.opBoolean","INTERSECT",EDGE,{"derivedFrom":[makeQuery(id+"F33.opExtrude","CAP_FACE",FACE,{"disambiguationData":[OSD([sQuery(id+"F0.wireOp",EDGE,"E0.top"),sQuery(id+"F0.wireOp",EDGE,"E1.bottom"),sQuery(id+"F0.wireOp",EDGE,"E1.top"),sQuery(id+"F0.wireOp",EDGE,"E1.left"),sQuery(id+"F0.wireOp",EDGE,"E1.right"),sQuery(id+"F0.wireOp",EDGE,"E4.bottom"),sQuery(id+"F0.wireOp",EDGE,"E4.top"),sQuery(id+"F0.wireOp",EDGE,"E4.left"),sQuery(id+"F0.wireOp",EDGE,"E4.right"),sQuery(id+"F0.wireOp",EDGE,"E6.bottom"),sQuery(id+"F0.wireOp",EDGE,"E6.top"),sQuery(id+"F0.wireOp",EDGE,"E6.left"),sQuery(id+"F0.wireOp",EDGE,"E6.right"),sQuery(id+"F21.wireOp",EDGE,"E25.bottom"),sQuery(id+"F25.wireOp",EDGE,"E26"),sQuery(id+"F32.wireOp",EDGE,"E31.bottom"),sQuery(id+"F32.wireOp",EDGE,"E31.left"),sQuery(id+"F32.wireOp",EDGE,"E31.right")])],"isStart":false}),makeQuery(id+"F37.opExtrude","SWEPT_FACE",FACE,{"disambiguationData":[OSD([sQuery(id+"F34.wireOp",EDGE,"E33.top")])]})]});
            var Q2;
            Q2=makeQuery(id+"F37.boolean.opBoolean","INTERSECT",EDGE,{"derivedFrom":[makeQuery(id+"F33.opExtrude","CAP_FACE",FACE,{"disambiguationData":[OSD([sQuery(id+"F0.wireOp",EDGE,"E0.top"),sQuery(id+"F0.wireOp",EDGE,"E1.bottom"),sQuery(id+"F0.wireOp",EDGE,"E1.top"),sQuery(id+"F0.wireOp",EDGE,"E1.left"),sQuery(id+"F0.wireOp",EDGE,"E1.right"),sQuery(id+"F0.wireOp",EDGE,"E4.bottom"),sQuery(id+"F0.wireOp",EDGE,"E4.top"),sQuery(id+"F0.wireOp",EDGE,"E4.left"),sQuery(id+"F0.wireOp",EDGE,"E4.right"),sQuery(id+"F0.wireOp",EDGE,"E6.bottom"),sQuery(id+"F0.wireOp",EDGE,"E6.top"),sQuery(id+"F0.wireOp",EDGE,"E6.left"),sQuery(id+"F0.wireOp",EDGE,"E6.right"),sQuery(id+"F21.wireOp",EDGE,"E25.bottom"),sQuery(id+"F25.wireOp",EDGE,"E26"),sQuery(id+"F32.wireOp",EDGE,"E31.bottom"),sQuery(id+"F32.wireOp",EDGE,"E31.left"),sQuery(id+"F32.wireOp",EDGE,"E31.right")])],"isStart":false}),makeQuery(id+"F37.opExtrude","SWEPT_FACE",FACE,{"disambiguationData":[OSD([sQuery(id+"F34.wireOp",EDGE,"E33.left")])]})]});
            var Q3;
            Q3=makeQuery(id+"F37.boolean.opBoolean","INTERSECT",EDGE,{"derivedFrom":[makeQuery(id+"F33.opExtrude","CAP_FACE",FACE,{"disambiguationData":[OSD([sQuery(id+"F0.wireOp",EDGE,"E0.top"),sQuery(id+"F0.wireOp",EDGE,"E1.bottom"),sQuery(id+"F0.wireOp",EDGE,"E1.top"),sQuery(id+"F0.wireOp",EDGE,"E1.left"),sQuery(id+"F0.wireOp",EDGE,"E1.right"),sQuery(id+"F0.wireOp",EDGE,"E4.bottom"),sQuery(id+"F0.wireOp",EDGE,"E4.top"),sQuery(id+"F0.wireOp",EDGE,"E4.left"),sQuery(id+"F0.wireOp",EDGE,"E4.right"),sQuery(id+"F0.wireOp",EDGE,"E6.bottom"),sQuery(id+"F0.wireOp",EDGE,"E6.top"),sQuery(id+"F0.wireOp",EDGE,"E6.left"),sQuery(id+"F0.wireOp",EDGE,"E6.right"),sQuery(id+"F21.wireOp",EDGE,"E25.bottom"),sQuery(id+"F25.wireOp",EDGE,"E26"),sQuery(id+"F32.wireOp",EDGE,"E31.bottom"),sQuery(id+"F32.wireOp",EDGE,"E31.left"),sQuery(id+"F32.wireOp",EDGE,"E31.right")])],"isStart":false}),makeQuery(id+"F37.opExtrude","SWEPT_FACE",FACE,{"disambiguationData":[OSD([sQuery(id+"F34.wireOp",EDGE,"E33.bottom")])]})]});
            var Q4;
            Q4=makeQuery(id+"F37.boolean.opBoolean","INTERSECT",EDGE,{"derivedFrom":[makeQuery(id+"F35.boolean.opBoolean","COPY",FACE,{"derivedFrom":makeQuery(id+"F35.opExtrude","CAP_FACE",FACE,{"disambiguationData":[OSD([sQuery(id+"F34.wireOp",EDGE,"E32.bottom"),sQuery(id+"F34.wireOp",EDGE,"E32.top"),sQuery(id+"F34.wireOp",EDGE,"E32.left"),sQuery(id+"F34.wireOp",EDGE,"E32.right")])],"isStart":false})}),makeQuery(id+"F37.opExtrude","SWEPT_FACE",FACE,{"disambiguationData":[OSD([sQuery(id+"F34.wireOp",EDGE,"E33.right")])]})]});
            var Q5;
            Q5=makeQuery(id+"F37.boolean.opBoolean","INTERSECT",EDGE,{"derivedFrom":[makeQuery(id+"F35.boolean.opBoolean","COPY",FACE,{"derivedFrom":makeQuery(id+"F35.opExtrude","CAP_FACE",FACE,{"disambiguationData":[OSD([sQuery(id+"F34.wireOp",EDGE,"E32.bottom"),sQuery(id+"F34.wireOp",EDGE,"E32.top"),sQuery(id+"F34.wireOp",EDGE,"E32.left"),sQuery(id+"F34.wireOp",EDGE,"E32.right")])],"isStart":false})}),makeQuery(id+"F37.opExtrude","SWEPT_FACE",FACE,{"disambiguationData":[OSD([sQuery(id+"F34.wireOp",EDGE,"E33.top")])]})]});
            var Q6;
            Q6=makeQuery(id+"F37.boolean.opBoolean","INTERSECT",EDGE,{"derivedFrom":[makeQuery(id+"F35.boolean.opBoolean","COPY",FACE,{"derivedFrom":makeQuery(id+"F35.opExtrude","CAP_FACE",FACE,{"disambiguationData":[OSD([sQuery(id+"F34.wireOp",EDGE,"E32.bottom"),sQuery(id+"F34.wireOp",EDGE,"E32.top"),sQuery(id+"F34.wireOp",EDGE,"E32.left"),sQuery(id+"F34.wireOp",EDGE,"E32.right")])],"isStart":false})}),makeQuery(id+"F37.opExtrude","SWEPT_FACE",FACE,{"disambiguationData":[OSD([sQuery(id+"F34.wireOp",EDGE,"E33.left")])]})]});
            var Q7;
            Q7=makeQuery(id+"F37.boolean.opBoolean","INTERSECT",EDGE,{"derivedFrom":[makeQuery(id+"F35.boolean.opBoolean","COPY",FACE,{"derivedFrom":makeQuery(id+"F35.opExtrude","CAP_FACE",FACE,{"disambiguationData":[OSD([sQuery(id+"F34.wireOp",EDGE,"E32.bottom"),sQuery(id+"F34.wireOp",EDGE,"E32.top"),sQuery(id+"F34.wireOp",EDGE,"E32.left"),sQuery(id+"F34.wireOp",EDGE,"E32.right")])],"isStart":false})}),makeQuery(id+"F37.opExtrude","SWEPT_FACE",FACE,{"disambiguationData":[OSD([sQuery(id+"F34.wireOp",EDGE,"E33.bottom")])]})]});
            var Q8;
            {var subQ0=sQuery(id+"F0.wireOp",EDGE,"E1.top");Q8=makeQuery(id+"F35.boolean.opBoolean","INTERSECT",EDGE,{"derivedFrom":[makeQuery(id+"F16.opFillet","BLEND_FACE",FACE,{"disambiguationData":[OSD([subQ0]),TDD([makeQuery(id+"F6.opExtrude","CAP_EDGE",EDGE,{"disambiguationData":[OSD([subQ0]),TDD([makeQuery(id+"F1.opExtrude","CAP_EDGE",EDGE,{"disambiguationData":[OSD([subQ0])],"isStart":true})])],"isStart":false})])]}),makeQuery(id+"F35.opExtrude","SWEPT_FACE",FACE,{"disambiguationData":[OSD([sQuery(id+"F34.wireOp",EDGE,"E32.right")])]})]});}
            var Q9;
            {var subQ0=sQuery(id+"F0.wireOp",EDGE,"E1.top");Q9=makeQuery(id+"F35.boolean.opBoolean","INTERSECT",EDGE,{"derivedFrom":[makeQuery(id+"F16.opFillet","BLEND_FACE",FACE,{"disambiguationData":[OSD([subQ0]),TDD([makeQuery(id+"F6.opExtrude","CAP_EDGE",EDGE,{"disambiguationData":[OSD([subQ0]),TDD([makeQuery(id+"F1.opExtrude","CAP_EDGE",EDGE,{"disambiguationData":[OSD([subQ0])],"isStart":true})])],"isStart":false})])]}),makeQuery(id+"F35.opExtrude","SWEPT_FACE",FACE,{"disambiguationData":[OSD([sQuery(id+"F34.wireOp",EDGE,"E32.top")])]})]});}
            var Q10;
            Q10=makeQuery(id+"F35.boolean.opBoolean","INTERSECT",EDGE,{"derivedFrom":[makeQuery(id+"F15.opFillet","BLEND_FACE",FACE,{"disambiguationData":[OSD([sQuery(id+"F0.wireOp",EDGE,"E1.top"),sQuery(id+"F0.wireOp",EDGE,"E1.left"),sQuery(id+"F7.wireOp",EDGE,"E12.top")])]}),makeQuery(id+"F35.opExtrude","SWEPT_FACE",FACE,{"disambiguationData":[OSD([sQuery(id+"F34.wireOp",EDGE,"E32.left")])]})]});
            var Q11;
            Q11=makeQuery(id+"F35.boolean.opBoolean","INTERSECT",EDGE,{"derivedFrom":[makeQuery(id+"F8.boolean.opBoolean","COPY",FACE,{"derivedFrom":makeQuery(id+"F8.opExtrude","SWEPT_FACE",FACE,{"disambiguationData":[OSD([sQuery(id+"F7.wireOp",EDGE,"E15.filletArc")])]})}),makeQuery(id+"F35.opExtrude","SWEPT_FACE",FACE,{"disambiguationData":[OSD([sQuery(id+"F34.wireOp",EDGE,"E32.bottom")])]})]});
            fillet(context, id + "F40", {"entities" : qUnion([Q0, Q1, Q2, Q3, Q4, Q5, Q6, Q7, Q8, Q9, Q10, Q11]), "radius" : 0.25 * mm, "tangentPropagation" : true, "allowEdgeOverflow" : false});
        }
    });
